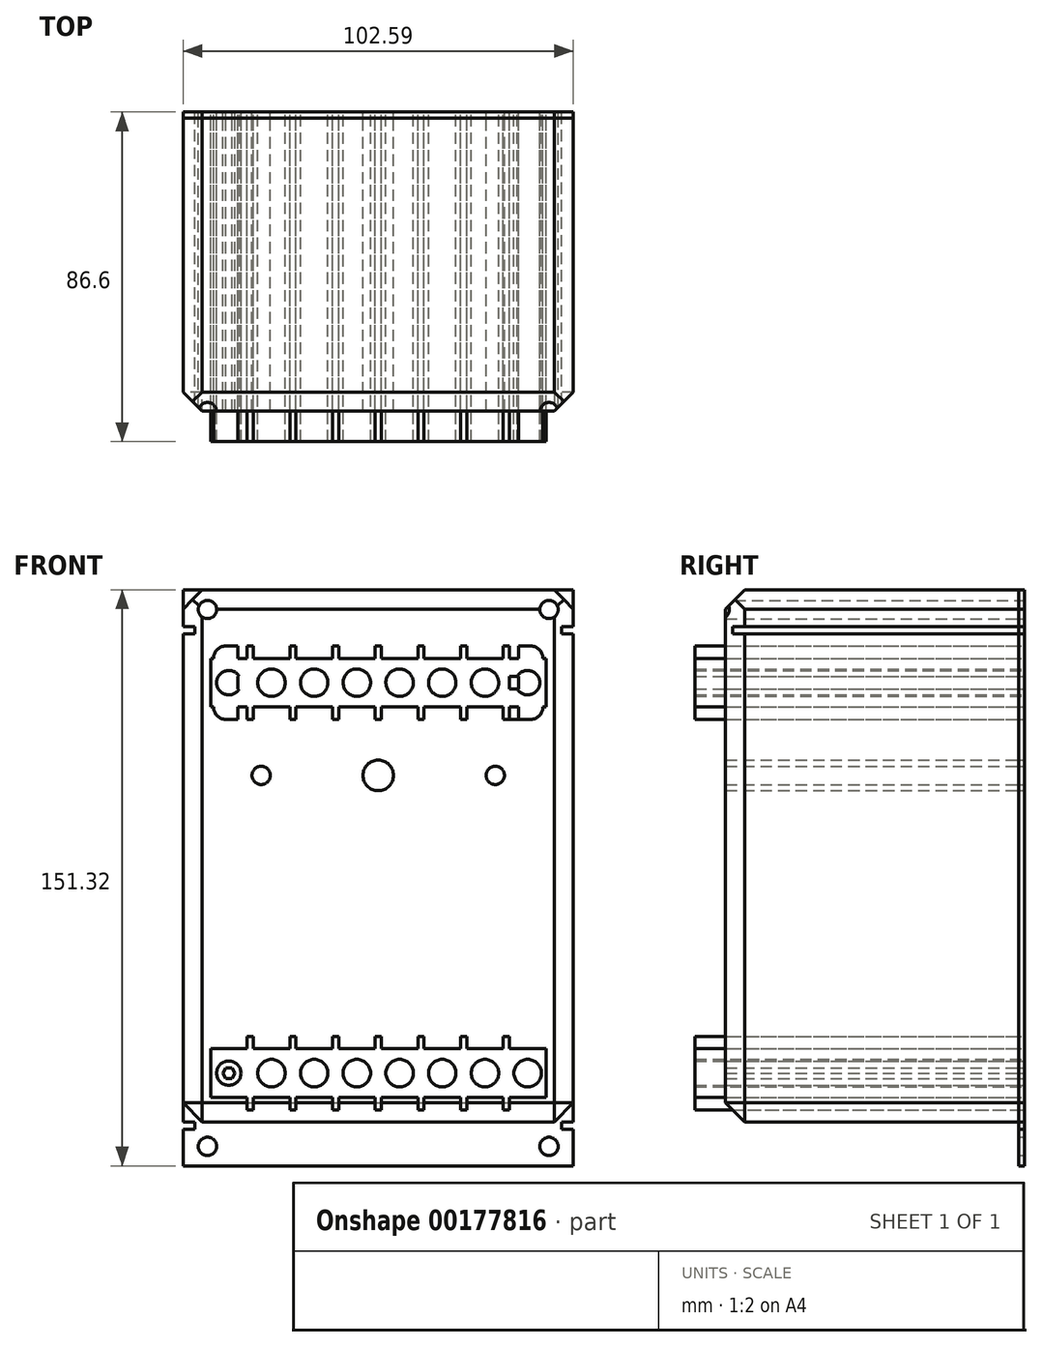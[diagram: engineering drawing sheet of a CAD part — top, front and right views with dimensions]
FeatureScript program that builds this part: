
annotation { "Feature Type Name" : "Feature", "Feature Type Description" : "" }
export const myFeature = defineFeature(function(context is Context, id is Id, definition is map)
    precondition{}
    {
        {
            var Q0;
            Q0=qCreatedBy(makeId("Front.planeOp"),FACE);
            var sketch = newSketch(context, id + "F0", { "sketchPlane" : qUnion([Q0])});
            skLineSegment(sketch, "E0", {"start": v(-127.7, 65.2) * mm, "end": v(-25.11, 65.2) * mm});
            skLineSegment(sketch, "E1", {"start": v(-25.11, 65.2) * mm, "end": v(-25.11, -63.04) * mm});
            skLineSegment(sketch, "E2", {"start": v(-25.11, -63.04) * mm, "end": v(-127.7, -63.04) * mm});
            skLineSegment(sketch, "E3", {"start": v(-127.7, -63.04) * mm, "end": v(-127.7, 65.2) * mm});
            skLineSegment(sketch, "E4", {"start": v(-127.7, 76.74) * mm, "end": v(-25.11, 76.74) * mm});
            skLineSegment(sketch, "E5", {"start": v(-25.11, -74.58) * mm, "end": v(-127.7, -74.58) * mm});
            skLineSegment(sketch, "E6", {"start": v(-127.7, 67.12) * mm, "end": v(-124.57, 67.12) * mm});
            skLineSegment(sketch, "E7", {"start": v(-25.11, -64.96) * mm, "end": v(-28.24, -64.96) * mm});
            skLineSegment(sketch, "E8", {"start": v(-124.57, -64.96) * mm, "end": v(-124.57, -63.04) * mm});
            skLineSegment(sketch, "E9", {"start": v(-28.24, -64.96) * mm, "end": v(-28.24, -63.04) * mm});
            skLineSegment(sketch, "E10", {"start": v(-127.7, 76.74) * mm, "end": v(-127.7, 67.12) * mm});
            skLineSegment(sketch, "E11", {"start": v(-124.57, 65.2) * mm, "end": v(-124.57, 67.12) * mm});
            skLineSegment(sketch, "E12", {"start": v(-28.24, 65.2) * mm, "end": v(-28.24, 67.12) * mm});
            skLineSegment(sketch, "E13", {"start": v(-25.11, 76.74) * mm, "end": v(-25.11, 67.12) * mm});
            skLineSegment(sketch, "E14", {"start": v(-28.24, 67.12) * mm, "end": v(-25.11, 67.12) * mm});
            skLineSegment(sketch, "E15", {"start": v(-127.7, -64.96) * mm, "end": v(-127.7, -74.58) * mm});
            skLineSegment(sketch, "E16", {"start": v(-25.11, -64.96) * mm, "end": v(-25.11, -74.58) * mm});
            skLineSegment(sketch, "E17", {"start": v(-124.57, -64.96) * mm, "end": v(-127.7, -64.96) * mm});
            skCircle(sketch, "E18", {"center": v(-121.29, 71.6) * mm, "radius": 2.41 * mm});
            skCircle(sketch, "E19", {"center": v(-31.52, 71.6) * mm, "radius": 2.41 * mm});
            skCircle(sketch, "E20", {"center": v(-121.29, -69.45) * mm, "radius": 2.41 * mm});
            skCircle(sketch, "E21", {"center": v(-31.52, -69.45) * mm, "radius": 2.41 * mm});
            skLineSegment(sketch, "E22", {"start": v(-102.11, 49.64) * mm, "end": v(-107.62, 54.1) * mm});
            skLineSegment(sketch, "E23", {"start": v(-101.3, 50.63) * mm, "end": v(-106.82, 55.1) * mm});
            skCircle(sketch, "E24", {"center": v(-104.46, 52.37) * mm, "radius": 3.6 * mm});
            skLineSegment(sketch, "E25", {"start": v(-90.88, 49.64) * mm, "end": v(-96.4, 54.1) * mm});
            skLineSegment(sketch, "E26", {"start": v(-90.07, 50.63) * mm, "end": v(-95.58, 55.1) * mm});
            skCircle(sketch, "E27", {"center": v(-93.23, 52.37) * mm, "radius": 3.6 * mm});
            skLineSegment(sketch, "E28", {"start": v(-79.67, 49.64) * mm, "end": v(-85.18, 54.1) * mm});
            skLineSegment(sketch, "E29", {"start": v(-78.86, 50.63) * mm, "end": v(-84.37, 55.1) * mm});
            skCircle(sketch, "E30", {"center": v(-82.02, 52.37) * mm, "radius": 3.6 * mm});
            skLineSegment(sketch, "E31", {"start": v(-68.44, 49.64) * mm, "end": v(-73.95, 54.1) * mm});
            skLineSegment(sketch, "E32", {"start": v(-67.63, 50.63) * mm, "end": v(-73.14, 55.1) * mm});
            skCircle(sketch, "E33", {"center": v(-70.79, 52.37) * mm, "radius": 3.6 * mm});
            skLineSegment(sketch, "E34", {"start": v(-57.23, 49.64) * mm, "end": v(-62.74, 54.1) * mm});
            skLineSegment(sketch, "E35", {"start": v(-56.42, 50.63) * mm, "end": v(-61.93, 55.1) * mm});
            skCircle(sketch, "E36", {"center": v(-59.58, 52.37) * mm, "radius": 3.6 * mm});
            skLineSegment(sketch, "E37", {"start": v(-46, 49.64) * mm, "end": v(-51.5, 54.1) * mm});
            skLineSegment(sketch, "E38", {"start": v(-45.19, 50.63) * mm, "end": v(-50.7, 55.1) * mm});
            skCircle(sketch, "E39", {"center": v(-48.35, 52.37) * mm, "radius": 3.6 * mm});
            skLineSegment(sketch, "E40", {"start": v(-120.47, 58.78) * mm, "end": v(-119.69, 58.78) * mm});
            skLineSegment(sketch, "E41", {"start": v(-120.47, 45.96) * mm, "end": v(-119.69, 45.96) * mm});
            skLineSegment(sketch, "E42", {"start": v(-110.87, 61.99) * mm, "end": v(-109.27, 61.99) * mm});
            skLineSegment(sketch, "E43", {"start": v(-110.87, 42.75) * mm, "end": v(-109.27, 42.75) * mm});
            skLineSegment(sketch, "E44", {"start": v(-109.27, 61.99) * mm, "end": v(-109.27, 42.75) * mm});
            skLineSegment(sketch, "E45", {"start": v(-110.87, 61.99) * mm, "end": v(-110.87, 42.75) * mm});
            skLineSegment(sketch, "E46", {"start": v(-98.03, 61.99) * mm, "end": v(-98.03, 42.75) * mm});
            skLineSegment(sketch, "E47", {"start": v(-99.64, 61.99) * mm, "end": v(-99.64, 42.75) * mm});
            skLineSegment(sketch, "E48", {"start": v(-88.43, 61.99) * mm, "end": v(-88.43, 42.75) * mm});
            skLineSegment(sketch, "E49", {"start": v(-86.83, 61.99) * mm, "end": v(-86.83, 42.75) * mm});
            skLineSegment(sketch, "E50", {"start": v(-77.2, 61.99) * mm, "end": v(-77.2, 42.75) * mm});
            skLineSegment(sketch, "E51", {"start": v(-75.6, 61.99) * mm, "end": v(-75.6, 42.75) * mm});
            skLineSegment(sketch, "E52", {"start": v(-65.99, 61.99) * mm, "end": v(-65.99, 42.75) * mm});
            skLineSegment(sketch, "E53", {"start": v(-64.38, 61.99) * mm, "end": v(-64.38, 42.75) * mm});
            skLineSegment(sketch, "E54", {"start": v(-54.75, 61.99) * mm, "end": v(-54.75, 42.75) * mm});
            skLineSegment(sketch, "E55", {"start": v(-53.15, 61.99) * mm, "end": v(-53.15, 42.75) * mm});
            skLineSegment(sketch, "E56", {"start": v(-43.55, 61.99) * mm, "end": v(-43.55, 42.75) * mm});
            skLineSegment(sketch, "E57", {"start": v(-41.94, 61.99) * mm, "end": v(-41.94, 42.75) * mm});
            skLineSegment(sketch, "E58", {"start": v(-120.47, 45.96) * mm, "end": v(-120.47, 58.78) * mm});
            skLineSegment(sketch, "E59", {"start": v(-32.34, 45.96) * mm, "end": v(-32.34, 58.78) * mm});
            skLineSegment(sketch, "E60", {"start": v(-41.94, 58.78) * mm, "end": v(-39.54, 58.78) * mm});
            skLineSegment(sketch, "E61", {"start": v(-43.55, 61.99) * mm, "end": v(-41.94, 61.99) * mm});
            skLineSegment(sketch, "E62", {"start": v(-53.15, 58.78) * mm, "end": v(-43.55, 58.78) * mm});
            skLineSegment(sketch, "E63", {"start": v(-54.75, 61.99) * mm, "end": v(-53.15, 61.99) * mm});
            skLineSegment(sketch, "E64", {"start": v(-64.38, 58.78) * mm, "end": v(-54.75, 58.78) * mm});
            skLineSegment(sketch, "E65", {"start": v(-65.99, 61.99) * mm, "end": v(-64.38, 61.99) * mm});
            skLineSegment(sketch, "E66", {"start": v(-75.6, 58.78) * mm, "end": v(-65.99, 58.78) * mm});
            skLineSegment(sketch, "E67", {"start": v(-77.2, 61.99) * mm, "end": v(-75.6, 61.99) * mm});
            skLineSegment(sketch, "E68", {"start": v(-86.83, 58.78) * mm, "end": v(-77.2, 58.78) * mm});
            skLineSegment(sketch, "E69", {"start": v(-88.43, 61.99) * mm, "end": v(-86.83, 61.99) * mm});
            skLineSegment(sketch, "E70", {"start": v(-98.03, 58.78) * mm, "end": v(-88.43, 58.78) * mm});
            skLineSegment(sketch, "E71", {"start": v(-99.64, 61.99) * mm, "end": v(-98.03, 61.99) * mm});
            skLineSegment(sketch, "E72", {"start": v(-109.27, 58.78) * mm, "end": v(-99.64, 58.78) * mm});
            skLineSegment(sketch, "E73", {"start": v(-99.64, 42.75) * mm, "end": v(-98.03, 42.75) * mm});
            skLineSegment(sketch, "E74", {"start": v(-98.03, 45.96) * mm, "end": v(-88.43, 45.96) * mm});
            skLineSegment(sketch, "E75", {"start": v(-88.43, 42.75) * mm, "end": v(-86.83, 42.75) * mm});
            skLineSegment(sketch, "E76", {"start": v(-86.83, 45.96) * mm, "end": v(-77.2, 45.96) * mm});
            skLineSegment(sketch, "E77", {"start": v(-77.2, 42.75) * mm, "end": v(-75.6, 42.75) * mm});
            skLineSegment(sketch, "E78", {"start": v(-75.6, 45.96) * mm, "end": v(-65.99, 45.96) * mm});
            skLineSegment(sketch, "E79", {"start": v(-65.99, 42.75) * mm, "end": v(-64.38, 42.75) * mm});
            skLineSegment(sketch, "E80", {"start": v(-64.38, 45.96) * mm, "end": v(-54.75, 45.96) * mm});
            skLineSegment(sketch, "E81", {"start": v(-54.75, 42.75) * mm, "end": v(-53.15, 42.75) * mm});
            skLineSegment(sketch, "E82", {"start": v(-53.15, 45.96) * mm, "end": v(-43.55, 45.96) * mm});
            skLineSegment(sketch, "E83", {"start": v(-43.55, 42.75) * mm, "end": v(-41.94, 42.75) * mm});
            skLineSegment(sketch, "E84", {"start": v(-41.94, 45.96) * mm, "end": v(-39.54, 45.96) * mm});
            skLineSegment(sketch, "E85", {"start": v(-109.27, 45.96) * mm, "end": v(-99.64, 45.96) * mm});
            skLineSegment(sketch, "E86", {"start": v(-109.27, -56.63) * mm, "end": v(-99.64, -56.63) * mm});
            skLineSegment(sketch, "E87", {"start": v(-41.94, -56.63) * mm, "end": v(-32.34, -56.63) * mm});
            skLineSegment(sketch, "E88", {"start": v(-43.55, -59.84) * mm, "end": v(-41.94, -59.84) * mm});
            skLineSegment(sketch, "E89", {"start": v(-53.15, -56.63) * mm, "end": v(-43.55, -56.63) * mm});
            skLineSegment(sketch, "E90", {"start": v(-54.75, -59.84) * mm, "end": v(-53.15, -59.84) * mm});
            skLineSegment(sketch, "E91", {"start": v(-64.38, -56.63) * mm, "end": v(-54.75, -56.63) * mm});
            skLineSegment(sketch, "E92", {"start": v(-65.99, -59.84) * mm, "end": v(-64.38, -59.84) * mm});
            skLineSegment(sketch, "E93", {"start": v(-75.6, -56.63) * mm, "end": v(-65.99, -56.63) * mm});
            skLineSegment(sketch, "E94", {"start": v(-77.2, -59.84) * mm, "end": v(-75.6, -59.84) * mm});
            skLineSegment(sketch, "E95", {"start": v(-86.83, -56.63) * mm, "end": v(-77.2, -56.63) * mm});
            skLineSegment(sketch, "E96", {"start": v(-88.43, -59.84) * mm, "end": v(-86.83, -59.84) * mm});
            skLineSegment(sketch, "E97", {"start": v(-98.03, -56.63) * mm, "end": v(-88.43, -56.63) * mm});
            skLineSegment(sketch, "E98", {"start": v(-99.64, -59.84) * mm, "end": v(-98.03, -59.84) * mm});
            skLineSegment(sketch, "E99", {"start": v(-109.27, -43.8) * mm, "end": v(-99.64, -43.8) * mm});
            skLineSegment(sketch, "E100", {"start": v(-99.64, -40.6) * mm, "end": v(-98.03, -40.6) * mm});
            skLineSegment(sketch, "E101", {"start": v(-98.03, -43.8) * mm, "end": v(-88.43, -43.8) * mm});
            skLineSegment(sketch, "E102", {"start": v(-88.43, -40.6) * mm, "end": v(-86.83, -40.6) * mm});
            skLineSegment(sketch, "E103", {"start": v(-86.83, -43.8) * mm, "end": v(-77.2, -43.8) * mm});
            skLineSegment(sketch, "E104", {"start": v(-77.2, -40.6) * mm, "end": v(-75.6, -40.6) * mm});
            skLineSegment(sketch, "E105", {"start": v(-75.6, -43.8) * mm, "end": v(-65.99, -43.8) * mm});
            skLineSegment(sketch, "E106", {"start": v(-65.99, -40.6) * mm, "end": v(-64.38, -40.6) * mm});
            skLineSegment(sketch, "E107", {"start": v(-64.38, -43.8) * mm, "end": v(-54.75, -43.8) * mm});
            skLineSegment(sketch, "E108", {"start": v(-54.75, -40.6) * mm, "end": v(-53.15, -40.6) * mm});
            skLineSegment(sketch, "E109", {"start": v(-53.15, -43.8) * mm, "end": v(-43.55, -43.8) * mm});
            skLineSegment(sketch, "E110", {"start": v(-43.55, -40.6) * mm, "end": v(-41.94, -40.6) * mm});
            skLineSegment(sketch, "E111", {"start": v(-41.94, -43.8) * mm, "end": v(-32.34, -43.8) * mm});
            skLineSegment(sketch, "E112", {"start": v(-32.34, -56.63) * mm, "end": v(-32.34, -43.8) * mm});
            skLineSegment(sketch, "E113", {"start": v(-120.47, -56.63) * mm, "end": v(-120.47, -43.8) * mm});
            skLineSegment(sketch, "E114", {"start": v(-41.94, -40.6) * mm, "end": v(-41.94, -59.84) * mm});
            skLineSegment(sketch, "E115", {"start": v(-43.55, -40.6) * mm, "end": v(-43.55, -59.84) * mm});
            skLineSegment(sketch, "E116", {"start": v(-53.15, -40.6) * mm, "end": v(-53.15, -59.84) * mm});
            skLineSegment(sketch, "E117", {"start": v(-54.75, -40.6) * mm, "end": v(-54.75, -59.84) * mm});
            skLineSegment(sketch, "E118", {"start": v(-64.38, -40.6) * mm, "end": v(-64.38, -59.84) * mm});
            skLineSegment(sketch, "E119", {"start": v(-65.99, -40.6) * mm, "end": v(-65.99, -59.84) * mm});
            skLineSegment(sketch, "E120", {"start": v(-75.6, -40.6) * mm, "end": v(-75.6, -59.84) * mm});
            skLineSegment(sketch, "E121", {"start": v(-77.2, -40.6) * mm, "end": v(-77.2, -59.84) * mm});
            skLineSegment(sketch, "E122", {"start": v(-86.83, -40.6) * mm, "end": v(-86.83, -59.84) * mm});
            skLineSegment(sketch, "E123", {"start": v(-88.43, -40.6) * mm, "end": v(-88.43, -59.84) * mm});
            skLineSegment(sketch, "E124", {"start": v(-99.64, -40.6) * mm, "end": v(-99.64, -59.84) * mm});
            skLineSegment(sketch, "E125", {"start": v(-98.03, -40.6) * mm, "end": v(-98.03, -59.84) * mm});
            skLineSegment(sketch, "E126", {"start": v(-110.87, -40.6) * mm, "end": v(-110.87, -59.84) * mm});
            skLineSegment(sketch, "E127", {"start": v(-109.27, -40.6) * mm, "end": v(-109.27, -59.84) * mm});
            skLineSegment(sketch, "E128", {"start": v(-110.87, -59.84) * mm, "end": v(-109.27, -59.84) * mm});
            skLineSegment(sketch, "E129", {"start": v(-110.87, -40.6) * mm, "end": v(-109.27, -40.6) * mm});
            skLineSegment(sketch, "E130", {"start": v(-120.47, -56.63) * mm, "end": v(-110.87, -56.63) * mm});
            skLineSegment(sketch, "E131", {"start": v(-120.47, -43.8) * mm, "end": v(-110.87, -43.8) * mm});
            skCircle(sketch, "E132", {"center": v(-37.14, -50.22) * mm, "radius": 3.6 * mm});
            skLineSegment(sketch, "E133", {"start": v(-33.98, -51.96) * mm, "end": v(-39.5, -47.48) * mm});
            skLineSegment(sketch, "E134", {"start": v(-34.79, -52.95) * mm, "end": v(-40.3, -48.48) * mm});
            skCircle(sketch, "E135", {"center": v(-48.35, -50.22) * mm, "radius": 3.6 * mm});
            skLineSegment(sketch, "E136", {"start": v(-45.19, -51.96) * mm, "end": v(-50.7, -47.48) * mm});
            skLineSegment(sketch, "E137", {"start": v(-46, -52.95) * mm, "end": v(-51.5, -48.48) * mm});
            skCircle(sketch, "E138", {"center": v(-59.58, -50.22) * mm, "radius": 3.6 * mm});
            skLineSegment(sketch, "E139", {"start": v(-56.42, -51.96) * mm, "end": v(-61.93, -47.48) * mm});
            skLineSegment(sketch, "E140", {"start": v(-57.23, -52.95) * mm, "end": v(-62.74, -48.48) * mm});
            skCircle(sketch, "E141", {"center": v(-70.79, -50.22) * mm, "radius": 3.6 * mm});
            skLineSegment(sketch, "E142", {"start": v(-67.63, -51.96) * mm, "end": v(-73.14, -47.48) * mm});
            skLineSegment(sketch, "E143", {"start": v(-68.44, -52.95) * mm, "end": v(-73.95, -48.48) * mm});
            skCircle(sketch, "E144", {"center": v(-82.02, -50.22) * mm, "radius": 3.6 * mm});
            skLineSegment(sketch, "E145", {"start": v(-78.86, -51.96) * mm, "end": v(-84.37, -47.48) * mm});
            skLineSegment(sketch, "E146", {"start": v(-79.67, -52.95) * mm, "end": v(-85.18, -48.48) * mm});
            skCircle(sketch, "E147", {"center": v(-93.23, -50.22) * mm, "radius": 3.6 * mm});
            skLineSegment(sketch, "E148", {"start": v(-90.07, -51.96) * mm, "end": v(-95.58, -47.48) * mm});
            skLineSegment(sketch, "E149", {"start": v(-90.88, -52.95) * mm, "end": v(-96.4, -48.48) * mm});
            skCircle(sketch, "E150", {"center": v(-104.46, -50.22) * mm, "radius": 3.6 * mm});
            skLineSegment(sketch, "E151", {"start": v(-101.3, -51.96) * mm, "end": v(-106.82, -47.48) * mm});
            skLineSegment(sketch, "E152", {"start": v(-102.11, -52.95) * mm, "end": v(-107.62, -48.48) * mm});
            skCircle(sketch, "E153", {"center": v(-107.18, 28) * mm, "radius": 4 * mm});
            skCircle(sketch, "E154", {"center": v(-107.18, 28) * mm, "radius": 2.4 * mm});
            skCircle(sketch, "E155", {"center": v(-45.63, 28) * mm, "radius": 4 * mm});
            skCircle(sketch, "E156", {"center": v(-45.63, 28) * mm, "radius": 2.4 * mm});
            skCircle(sketch, "E157", {"center": v(-76.4, 28) * mm, "radius": 4 * mm});
            skCircle(sketch, "E158", {"center": v(-107.18, 1.08) * mm, "radius": 3.6 * mm});
            skLineSegment(sketch, "E159", {"start": v(-81.92, 12.95) * mm, "end": v(-81.92, 2.03) * mm});
            skLineSegment(sketch, "E160", {"start": v(-70.9, 12.95) * mm, "end": v(-70.9, 2.03) * mm});
            skLineSegment(sketch, "E161", {"start": v(-81.92, 12.95) * mm, "end": v(-70.9, 12.95) * mm});
            skLineSegment(sketch, "E162", {"start": v(-81.92, 2.03) * mm, "end": v(-70.9, 2.03) * mm});
            skCircle(sketch, "E163", {"center": v(-115.67, -50.22) * mm, "radius": 3.2 * mm});
            skLineSegment(sketch, "E164", {"start": v(-116.47, -48.83) * mm, "end": v(-117.27, -50.22) * mm});
            skLineSegment(sketch, "E165", {"start": v(-117.27, -50.22) * mm, "end": v(-116.47, -51.6) * mm});
            skLineSegment(sketch, "E166", {"start": v(-116.47, -51.6) * mm, "end": v(-114.87, -51.6) * mm});
            skLineSegment(sketch, "E167", {"start": v(-114.87, -51.6) * mm, "end": v(-114.07, -50.22) * mm});
            skLineSegment(sketch, "E168", {"start": v(-114.07, -50.22) * mm, "end": v(-114.87, -48.83) * mm});
            skLineSegment(sketch, "E169", {"start": v(-114.87, -48.83) * mm, "end": v(-116.47, -48.83) * mm});
            skArc(sketch, "E170", {"start": v(-112.9, 53.97) * mm, "mid": v(-118.88, 52.37) * mm, "end": v(-112.9, 50.77) * mm});
            skLineSegment(sketch, "E171", {"start": v(-116.47, 53.76) * mm, "end": v(-117.27, 52.37) * mm});
            skLineSegment(sketch, "E172", {"start": v(-117.27, 52.37) * mm, "end": v(-116.47, 50.98) * mm});
            skLineSegment(sketch, "E173", {"start": v(-116.47, 50.98) * mm, "end": v(-114.87, 50.98) * mm});
            skLineSegment(sketch, "E174", {"start": v(-114.87, 50.98) * mm, "end": v(-114.07, 52.37) * mm});
            skLineSegment(sketch, "E175", {"start": v(-114.07, 52.37) * mm, "end": v(-114.87, 53.76) * mm});
            skLineSegment(sketch, "E176", {"start": v(-114.87, 53.76) * mm, "end": v(-116.47, 53.76) * mm});
            skArc(sketch, "E177", {"start": v(-39.92, 50.77) * mm, "mid": v(-33.93, 52.37) * mm, "end": v(-39.92, 53.97) * mm});
            skLineSegment(sketch, "E178", {"start": v(-37.94, 53.76) * mm, "end": v(-38.74, 52.37) * mm});
            skLineSegment(sketch, "E179", {"start": v(-38.74, 52.37) * mm, "end": v(-37.94, 50.98) * mm});
            skLineSegment(sketch, "E180", {"start": v(-37.94, 50.98) * mm, "end": v(-36.34, 50.98) * mm});
            skLineSegment(sketch, "E181", {"start": v(-36.34, 50.98) * mm, "end": v(-35.54, 52.37) * mm});
            skLineSegment(sketch, "E182", {"start": v(-35.54, 52.37) * mm, "end": v(-36.34, 53.76) * mm});
            skLineSegment(sketch, "E183", {"start": v(-36.34, 53.76) * mm, "end": v(-37.94, 53.76) * mm});
            skLineSegment(sketch, "E184", {"start": v(-107.18, 4.68) * mm, "end": v(-107.18, 7.41) * mm});
            skLineSegment(sketch, "E185", {"start": v(-110.61, 2.2) * mm, "end": v(-113.21, 3.04) * mm});
            skLineSegment(sketch, "E186", {"start": v(-109.3, -1.84) * mm, "end": v(-110.9, -4.05) * mm});
            skLineSegment(sketch, "E187", {"start": v(-105.06, -1.84) * mm, "end": v(-103.46, -4.05) * mm});
            skLineSegment(sketch, "E188", {"start": v(-103.75, 2.2) * mm, "end": v(-101.16, 3.04) * mm});
            skLineSegment(sketch, "E189", {"start": v(41.36, 42.75) * mm, "end": v(49.78, 42.11) * mm});
            skLineSegment(sketch, "E190", {"start": v(41.36, 55.58) * mm, "end": v(49.78, 56.22) * mm});
            skLineSegment(sketch, "E191", {"start": v(34.52, 50.77) * mm, "end": v(34.52, 55.58) * mm});
            skLineSegment(sketch, "E192", {"start": v(32.55, 39.55) * mm, "end": v(39.76, 39.55) * mm});
            skLineSegment(sketch, "E193", {"start": v(32.55, 58.78) * mm, "end": v(39.68, 58.78) * mm});
            skLineSegment(sketch, "E194", {"start": v(29.34, 55.58) * mm, "end": v(29.34, 58.78) * mm});
            skLineSegment(sketch, "E195", {"start": v(29.34, 47.56) * mm, "end": v(29.34, 50.77) * mm});
            skLineSegment(sketch, "E196", {"start": v(32.55, 39.55) * mm, "end": v(32.55, 42.75) * mm});
            skLineSegment(sketch, "E197", {"start": v(29.34, 39.55) * mm, "end": v(29.34, 42.75) * mm});
            skLineSegment(sketch, "E198", {"start": v(41.36, 39.55) * mm, "end": v(44.25, 39.55) * mm});
            skLineSegment(sketch, "E199", {"start": v(41.36, 39.55) * mm, "end": v(41.36, 58.78) * mm});
            skLineSegment(sketch, "E200", {"start": v(29.34, 39.55) * mm, "end": v(32.55, 39.55) * mm});
            skLineSegment(sketch, "E201", {"start": v(29.34, 42.75) * mm, "end": v(39.76, 42.75) * mm});
            skLineSegment(sketch, "E202", {"start": v(29.34, 47.56) * mm, "end": v(36.82, 47.56) * mm});
            skLineSegment(sketch, "E203", {"start": v(29.34, 50.77) * mm, "end": v(36.82, 50.77) * mm});
            skLineSegment(sketch, "E204", {"start": v(29.34, 55.58) * mm, "end": v(39.76, 55.58) * mm});
            skLineSegment(sketch, "E205", {"start": v(29.34, 58.78) * mm, "end": v(32.55, 58.78) * mm});
            skLineSegment(sketch, "E206", {"start": v(-113.27, 50.77) * mm, "end": v(-110.87, 50.77) * mm});
            skLineSegment(sketch, "E207", {"start": v(-113.27, 53.97) * mm, "end": v(-110.87, 53.97) * mm});
            skLineSegment(sketch, "E208", {"start": v(-41.94, 53.97) * mm, "end": v(-41.94, 50.77) * mm});
            skLineSegment(sketch, "E209", {"start": v(-39.54, 53.97) * mm, "end": v(-39.54, 50.77) * mm});
            skLineSegment(sketch, "E210", {"start": v(-41.94, 45.96) * mm, "end": v(-41.94, 42.75) * mm});
            skLineSegment(sketch, "E211", {"start": v(-39.54, 45.96) * mm, "end": v(-39.54, 42.75) * mm});
            skLineSegment(sketch, "E212", {"start": v(-39.54, 42.75) * mm, "end": v(-41.94, 42.75) * mm});
            skLineSegment(sketch, "E213", {"start": v(-39.54, 61.99) * mm, "end": v(-41.94, 61.99) * mm});
            skLineSegment(sketch, "E214", {"start": v(-113.27, 53.97) * mm, "end": v(-113.27, 50.77) * mm});
            skLineSegment(sketch, "E215", {"start": v(-113.27, 45.96) * mm, "end": v(-113.27, 42.75) * mm});
            skLineSegment(sketch, "E216", {"start": v(-110.87, 45.96) * mm, "end": v(-110.87, 42.75) * mm});
            skLineSegment(sketch, "E217", {"start": v(-110.87, 53.97) * mm, "end": v(-110.87, 50.77) * mm});
            skLineSegment(sketch, "E218", {"start": v(-41.94, 50.77) * mm, "end": v(-39.54, 50.77) * mm});
            skLineSegment(sketch, "E219", {"start": v(-41.94, 53.97) * mm, "end": v(-39.54, 53.97) * mm});
            skLineSegment(sketch, "E220", {"start": v(-113.27, 45.96) * mm, "end": v(-110.87, 45.96) * mm});
            skLineSegment(sketch, "E221", {"start": v(-113.27, 58.78) * mm, "end": v(-110.87, 58.78) * mm});
            skLineSegment(sketch, "E222", {"start": v(-113.27, 42.75) * mm, "end": v(-110.87, 42.75) * mm});
            skLineSegment(sketch, "E223", {"start": v(-113.27, 61.99) * mm, "end": v(-110.87, 61.99) * mm});
            skLineSegment(sketch, "E224", {"start": v(-110.87, 61.99) * mm, "end": v(-110.87, 58.78) * mm});
            skLineSegment(sketch, "E225", {"start": v(-41.94, 61.99) * mm, "end": v(-41.94, 58.78) * mm});
            skArc(sketch, "E226", {"start": v(-119.69, 45.96) * mm, "mid": v(-118.75, 43.7) * mm, "end": v(-116.48, 42.75) * mm});
            skArc(sketch, "E227", {"start": v(-36.33, 42.75) * mm, "mid": v(-34.07, 43.7) * mm, "end": v(-33.13, 45.96) * mm});
            skArc(sketch, "E228", {"start": v(-33.13, 58.78) * mm, "mid": v(-34.07, 61.05) * mm, "end": v(-36.33, 61.99) * mm});
            skArc(sketch, "E229", {"start": v(-116.48, 61.99) * mm, "mid": v(-118.75, 61.05) * mm, "end": v(-119.69, 58.78) * mm});
            skLineSegment(sketch, "E230", {"start": v(-119.69, 58.78) * mm, "end": v(-119.69, 45.96) * mm});
            skLineSegment(sketch, "E231", {"start": v(-33.13, 58.78) * mm, "end": v(-33.13, 45.96) * mm});
            skLineSegment(sketch, "E232", {"start": v(-113.27, 61.99) * mm, "end": v(-113.27, 58.78) * mm});
            skLineSegment(sketch, "E233", {"start": v(-39.54, 61.99) * mm, "end": v(-39.54, 58.78) * mm});
            skArc(sketch, "E234", {"start": v(38.15, 52.77) * mm, "mid": v(36.55, 49.16) * mm, "end": v(38.15, 45.56) * mm});
            skLineSegment(sketch, "E235", {"start": v(34.52, 42.75) * mm, "end": v(34.52, 47.56) * mm});
            skLineSegment(sketch, "E236", {"start": v(39.76, 39.55) * mm, "end": v(39.76, 58.78) * mm});
            skLineSegment(sketch, "E237", {"start": v(38.15, 45.56) * mm, "end": v(39.76, 45.56) * mm});
            skLineSegment(sketch, "E238", {"start": v(38.15, 52.77) * mm, "end": v(39.76, 52.77) * mm});
            skLineSegment(sketch, "E239", {"start": v(35.75, 39.55) * mm, "end": v(49.78, 39.55) * mm});
            skLineSegment(sketch, "E240", {"start": v(35.75, 58.78) * mm, "end": v(49.78, 58.78) * mm});
            skLineSegment(sketch, "E241", {"start": v(126.73, -64.96) * mm, "end": v(128.32, -64.96) * mm});
            skLineSegment(sketch, "E242", {"start": v(126.73, 67.12) * mm, "end": v(128.32, 67.12) * mm});
            skLineSegment(sketch, "E243", {"start": v(126.73, 55.58) * mm, "end": v(126.73, 76.74) * mm});
            skLineSegment(sketch, "E244", {"start": v(59.4, -52.15) * mm, "end": v(59.4, 54.3) * mm});
            skLineSegment(sketch, "E245", {"start": v(60.67, -53.42) * mm, "end": v(68.4, -53.42) * mm});
            skLineSegment(sketch, "E246", {"start": v(60.67, -53.42) * mm, "end": v(126.73, -53.42) * mm});
            skLineSegment(sketch, "E247", {"start": v(60.67, -53.42) * mm, "end": v(52.17, -61.93) * mm});
            skLineSegment(sketch, "E248", {"start": v(59.4, -52.15) * mm, "end": v(50.9, -60.66) * mm});
            skLineSegment(sketch, "E249", {"start": v(50.9, -61.93) * mm, "end": v(52.17, -61.93) * mm});
            skLineSegment(sketch, "E250", {"start": v(50.9, -61.93) * mm, "end": v(50.9, -60.66) * mm});
            skCircle(sketch, "E251", {"center": v(81.2, -58.23) * mm, "radius": 4.4 * mm});
            skCircle(sketch, "E252", {"center": v(81.2, -58.23) * mm, "radius": 3.62 * mm});
            skLineSegment(sketch, "E253", {"start": v(80.6, -59.27) * mm, "end": v(80, -58.23) * mm});
            skLineSegment(sketch, "E254", {"start": v(80, -58.23) * mm, "end": v(80.6, -57.2) * mm});
            skLineSegment(sketch, "E255", {"start": v(80.6, -57.2) * mm, "end": v(81.8, -57.2) * mm});
            skLineSegment(sketch, "E256", {"start": v(81.8, -57.2) * mm, "end": v(82.4, -58.23) * mm});
            skLineSegment(sketch, "E257", {"start": v(82.4, -58.23) * mm, "end": v(81.8, -59.27) * mm});
            skLineSegment(sketch, "E258", {"start": v(81.8, -59.27) * mm, "end": v(80.6, -59.27) * mm});
            skLineSegment(sketch, "E259", {"start": v(60.67, 55.58) * mm, "end": v(126.73, 55.58) * mm});
            skLineSegment(sketch, "E260", {"start": v(80.6, 61.43) * mm, "end": v(80, 60.39) * mm});
            skLineSegment(sketch, "E261", {"start": v(80, 60.39) * mm, "end": v(80.6, 59.34) * mm});
            skLineSegment(sketch, "E262", {"start": v(80.6, 59.34) * mm, "end": v(81.8, 59.34) * mm});
            skLineSegment(sketch, "E263", {"start": v(81.8, 59.34) * mm, "end": v(82.4, 60.39) * mm});
            skLineSegment(sketch, "E264", {"start": v(82.4, 60.39) * mm, "end": v(81.8, 61.43) * mm});
            skLineSegment(sketch, "E265", {"start": v(81.8, 61.43) * mm, "end": v(80.6, 61.43) * mm});
            skCircle(sketch, "E266", {"center": v(81.2, 60.39) * mm, "radius": 3.62 * mm});
            skCircle(sketch, "E267", {"center": v(81.2, 60.39) * mm, "radius": 4.4 * mm});
            skLineSegment(sketch, "E268", {"start": v(50.9, 64.08) * mm, "end": v(50.9, 62.81) * mm});
            skLineSegment(sketch, "E269", {"start": v(50.9, 64.08) * mm, "end": v(52.17, 64.08) * mm});
            skLineSegment(sketch, "E270", {"start": v(59.4, 54.3) * mm, "end": v(50.9, 62.81) * mm});
            skLineSegment(sketch, "E271", {"start": v(60.67, 55.58) * mm, "end": v(52.17, 64.08) * mm});
            skLineSegment(sketch, "E272", {"start": v(49.78, -63.04) * mm, "end": v(49.78, 65.2) * mm});
            skLineSegment(sketch, "E273", {"start": v(49.78, -63.04) * mm, "end": v(126.73, -63.04) * mm});
            skLineSegment(sketch, "E274", {"start": v(49.78, 65.2) * mm, "end": v(126.73, 65.2) * mm});
            skLineSegment(sketch, "E275", {"start": v(126.73, -74.58) * mm, "end": v(126.73, -53.42) * mm});
            skLineSegment(sketch, "E276", {"start": v(128.32, -74.58) * mm, "end": v(128.32, 76.74) * mm});
            skLineSegment(sketch, "E277", {"start": v(126.73, -74.58) * mm, "end": v(128.32, -74.58) * mm});
            skLineSegment(sketch, "E278", {"start": v(126.73, 76.74) * mm, "end": v(128.32, 76.74) * mm});
            skLineSegment(sketch, "E279", {"start": v(-116.48, 61.99) * mm, "end": v(-113.27, 61.99) * mm});
            skLineSegment(sketch, "E280", {"start": v(-116.48, 42.75) * mm, "end": v(-113.27, 42.75) * mm});
            skLineSegment(sketch, "E281", {"start": v(-36.33, 61.99) * mm, "end": v(-39.54, 61.99) * mm});
            skLineSegment(sketch, "E282", {"start": v(-36.33, 42.75) * mm, "end": v(-39.54, 42.75) * mm});
            skLineSegment(sketch, "E283", {"start": v(-33.13, 45.96) * mm, "end": v(-32.34, 45.96) * mm});
            skLineSegment(sketch, "E284", {"start": v(-33.13, 58.78) * mm, "end": v(-32.34, 58.78) * mm});
            skLineSegment(sketch, "E285", {"start": v(-111.64, 58.78) * mm, "end": v(-111.64, 53.97) * mm});
            skLineSegment(sketch, "E286", {"start": v(-41.17, 58.78) * mm, "end": v(-41.17, 53.97) * mm});
            skLineSegment(sketch, "E287", {"start": v(-41.17, 50.77) * mm, "end": v(-41.17, 45.96) * mm});
            skLineSegment(sketch, "E288", {"start": v(-111.64, 50.77) * mm, "end": v(-111.64, 45.96) * mm});
            skLineSegment(sketch, "E289", {"start": v(35.8, -40.6) * mm, "end": v(49.78, -40.6) * mm});
            skLineSegment(sketch, "E290", {"start": v(35.8, -59.84) * mm, "end": v(49.78, -59.84) * mm});
            skLineSegment(sketch, "E291", {"start": v(38.15, -46.61) * mm, "end": v(39.76, -46.61) * mm});
            skLineSegment(sketch, "E292", {"start": v(38.15, -53.82) * mm, "end": v(39.76, -53.82) * mm});
            skLineSegment(sketch, "E293", {"start": v(36.87, -51.96) * mm, "end": v(38.15, -51.96) * mm});
            skLineSegment(sketch, "E294", {"start": v(37.4, -52.95) * mm, "end": v(38.15, -52.95) * mm});
            skLineSegment(sketch, "E295", {"start": v(38.15, -52.95) * mm, "end": v(38.15, -51.96) * mm});
            skArc(sketch, "E296", {"start": v(38.15, -46.61) * mm, "mid": v(36.55, -50.22) * mm, "end": v(38.15, -53.82) * mm});
            skLineSegment(sketch, "E297", {"start": v(41.36, -56.63) * mm, "end": v(41.36, -43.8) * mm});
            skLineSegment(sketch, "E298", {"start": v(34.52, -58.55) * mm, "end": v(34.52, -41.88) * mm});
            skLineSegment(sketch, "E299", {"start": v(41.36, -43.8) * mm, "end": v(49.78, -43.16) * mm});
            skLineSegment(sketch, "E300", {"start": v(41.36, -56.63) * mm, "end": v(49.78, -57.27) * mm});
            skLineSegment(sketch, "E301", {"start": v(39.76, -46.61) * mm, "end": v(39.76, -53.88) * mm});
            skLineSegment(sketch, "E302", {"start": v(39.94, -46.61) * mm, "end": v(39.94, -53.88) * mm});
            skLineSegment(sketch, "E303", {"start": v(39.94, -46.61) * mm, "end": v(41.36, -46.61) * mm});
            skLineSegment(sketch, "E304", {"start": v(39.94, -53.88) * mm, "end": v(41.36, -53.88) * mm});
            skLineSegment(sketch, "E305", {"start": v(39.94, -50.24) * mm, "end": v(41.36, -50.24) * mm});
            skArc(sketch, "E306", {"start": v(35.8, -40.6) * mm, "mid": v(34.9, -40.98) * mm, "end": v(34.52, -41.88) * mm});
            skArc(sketch, "E307", {"start": v(34.52, -58.55) * mm, "mid": v(34.9, -59.46) * mm, "end": v(35.8, -59.84) * mm});
            skLineSegment(sketch, "E308", {"start": v(32.55, 47.56) * mm, "end": v(32.55, 50.77) * mm});
            skLineSegment(sketch, "E309", {"start": v(32.55, 55.58) * mm, "end": v(32.55, 58.78) * mm});
            skLineSegment(sketch, "E310", {"start": v(-23.77, 64.66) * mm, "end": v(-25.11, 64.66) * mm});
            skLineSegment(sketch, "E311", {"start": v(-23.77, 56.11) * mm, "end": v(-25.11, 56.11) * mm});
            skLineSegment(sketch, "E312", {"start": v(-23.5, 64.4) * mm, "end": v(-23.5, 56.37) * mm});
            skArc(sketch, "E313", {"start": v(-23.5, 56.9) * mm, "mid": v(-21.9, 60.39) * mm, "end": v(-23.5, 63.87) * mm});
            skArc(sketch, "E314", {"start": v(-23.5, 64.4) * mm, "mid": v(-23.58, 64.58) * mm, "end": v(-23.77, 64.66) * mm});
            skArc(sketch, "E315", {"start": v(-23.77, 56.11) * mm, "mid": v(-23.58, 56.19) * mm, "end": v(-23.5, 56.37) * mm});
            skArc(sketch, "E316", {"start": v(-23.77, -62.5) * mm, "mid": v(-23.58, -62.43) * mm, "end": v(-23.5, -62.25) * mm});
            skArc(sketch, "E317", {"start": v(-23.5, -54.22) * mm, "mid": v(-23.58, -54.04) * mm, "end": v(-23.77, -53.96) * mm});
            skArc(sketch, "E318", {"start": v(-23.5, -61.72) * mm, "mid": v(-21.9, -58.23) * mm, "end": v(-23.5, -54.75) * mm});
            skLineSegment(sketch, "E319", {"start": v(-23.5, -54.22) * mm, "end": v(-23.5, -62.25) * mm});
            skLineSegment(sketch, "E320", {"start": v(-23.77, -62.5) * mm, "end": v(-25.11, -62.5) * mm});
            skLineSegment(sketch, "E321", {"start": v(-23.77, -53.96) * mm, "end": v(-25.11, -53.96) * mm});
            skLineSegment(sketch, "E322", {"start": v(-129.05, -53.96) * mm, "end": v(-127.7, -53.96) * mm});
            skLineSegment(sketch, "E323", {"start": v(-129.05, -62.5) * mm, "end": v(-127.7, -62.5) * mm});
            skLineSegment(sketch, "E324", {"start": v(-129.3, -54.22) * mm, "end": v(-129.3, -62.25) * mm});
            skArc(sketch, "E325", {"start": v(-129.3, -54.75) * mm, "mid": v(-130.9, -58.23) * mm, "end": v(-129.3, -61.72) * mm});
            skArc(sketch, "E326", {"start": v(-129.05, -53.96) * mm, "mid": v(-129.23, -54.04) * mm, "end": v(-129.3, -54.22) * mm});
            skArc(sketch, "E327", {"start": v(-129.3, -62.25) * mm, "mid": v(-129.23, -62.43) * mm, "end": v(-129.05, -62.5) * mm});
            skArc(sketch, "E328", {"start": v(-129.3, 56.37) * mm, "mid": v(-129.23, 56.19) * mm, "end": v(-129.05, 56.11) * mm});
            skArc(sketch, "E329", {"start": v(-129.05, 64.66) * mm, "mid": v(-129.23, 64.58) * mm, "end": v(-129.3, 64.4) * mm});
            skArc(sketch, "E330", {"start": v(-129.3, 63.87) * mm, "mid": v(-130.9, 60.39) * mm, "end": v(-129.3, 56.9) * mm});
            skLineSegment(sketch, "E331", {"start": v(-129.3, 64.4) * mm, "end": v(-129.3, 56.37) * mm});
            skLineSegment(sketch, "E332", {"start": v(-129.05, 56.11) * mm, "end": v(-127.7, 56.11) * mm});
            skLineSegment(sketch, "E333", {"start": v(-129.05, 64.66) * mm, "end": v(-127.7, 64.66) * mm});
            skLineSegment(sketch, "E334", {"start": v(-32.8, -69.45) * mm, "end": v(-30.24, -69.45) * mm});
            skLineSegment(sketch, "E335", {"start": v(-31.52, -70.74) * mm, "end": v(-31.52, -68.17) * mm});
            skLineSegment(sketch, "E336", {"start": v(-122.57, -69.45) * mm, "end": v(-120, -69.45) * mm});
            skLineSegment(sketch, "E337", {"start": v(-121.29, -70.74) * mm, "end": v(-121.29, -68.17) * mm});
            skLineSegment(sketch, "E338", {"start": v(-28.64, -69.45) * mm, "end": v(-26.4, -69.45) * mm});
            skLineSegment(sketch, "E339", {"start": v(48.76, 32.01) * mm, "end": v(49.78, 32.01) * mm});
            skLineSegment(sketch, "E340", {"start": v(48.76, 24) * mm, "end": v(49.78, 24) * mm});
            skLineSegment(sketch, "E341", {"start": v(46.57, 30.41) * mm, "end": v(48.76, 30.41) * mm});
            skLineSegment(sketch, "E342", {"start": v(46.57, 25.6) * mm, "end": v(48.76, 25.6) * mm});
            skLineSegment(sketch, "E343", {"start": v(48.76, 24) * mm, "end": v(48.76, 32.01) * mm});
            skArc(sketch, "E344", {"start": v(46.57, 30.41) * mm, "mid": v(45.02, 28) * mm, "end": v(46.57, 25.6) * mm});
            skLineSegment(sketch, "E345", {"start": v(47.73, 12.95) * mm, "end": v(49.78, 12.95) * mm});
            skLineSegment(sketch, "E346", {"start": v(47.73, 2.03) * mm, "end": v(49.78, 2.03) * mm});
            skLineSegment(sketch, "E347", {"start": v(48.55, -2.53) * mm, "end": v(48.55, 2.03) * mm});
            skLineSegment(sketch, "E348", {"start": v(47.73, 2.03) * mm, "end": v(47.73, 12.95) * mm});
            skLineSegment(sketch, "E349", {"start": v(48.55, -2.53) * mm, "end": v(49.78, -2.53) * mm});
            skLineSegment(sketch, "E350", {"start": v(47.32, -2.27) * mm, "end": v(48.55, -2.27) * mm});
            skLineSegment(sketch, "E351", {"start": v(47.32, -2.27) * mm, "end": v(47.32, 4.68) * mm});
            skLineSegment(sketch, "E352", {"start": v(47.32, 4.68) * mm, "end": v(47.73, 4.68) * mm});
            skArc(sketch, "E353", {"start": v(-109.17, -0.76) * mm, "mid": v(-108.99, -0.94) * mm, "end": v(-108.79, -1.1) * mm});
            skLineSegment(sketch, "E354", {"start": v(-109.17, -0.76) * mm, "end": v(-105.58, 3.26) * mm});
            skLineSegment(sketch, "E355", {"start": v(-108.79, -1.1) * mm, "end": v(-105.2, 2.91) * mm});
            skLineSegment(sketch, "E356", {"start": v(-108.57, 0.68) * mm, "end": v(-108.19, 0.34) * mm});
            skLineSegment(sketch, "E357", {"start": v(-108.57, 0.68) * mm, "end": v(-109.17, -0.76) * mm});
            skLineSegment(sketch, "E358", {"start": v(-107.42, -0.34) * mm, "end": v(-108.79, -1.1) * mm});
            skLineSegment(sketch, "E359", {"start": v(-107.8, 0) * mm, "end": v(-107.42, -0.34) * mm});
            skLineSegment(sketch, "E360", {"start": v(-76.4, 12.95) * mm, "end": v(-76.4, 2.03) * mm});
            skLineSegment(sketch, "E361", {"start": v(-72.05, 10.39) * mm, "end": v(-72.05, 4.6) * mm});
            skLineSegment(sketch, "E362", {"start": v(-75.25, 10.39) * mm, "end": v(-75.25, 4.6) * mm});
            skLineSegment(sketch, "E363", {"start": v(-77.56, 10.39) * mm, "end": v(-77.56, 4.6) * mm});
            skLineSegment(sketch, "E364", {"start": v(-80.77, 10.39) * mm, "end": v(-80.77, 4.6) * mm});
            skLineSegment(sketch, "E365", {"start": v(-80.77, 10.39) * mm, "end": v(-77.56, 10.39) * mm});
            skLineSegment(sketch, "E366", {"start": v(-80.77, 4.6) * mm, "end": v(-77.56, 4.6) * mm});
            skLineSegment(sketch, "E367", {"start": v(-75.25, 10.39) * mm, "end": v(-72.05, 10.39) * mm});
            skLineSegment(sketch, "E368", {"start": v(-75.25, 4.6) * mm, "end": v(-72.05, 4.6) * mm});
            skLineSegment(sketch, "E369", {"start": v(-80.77, 6.52) * mm, "end": v(-77.56, 6.52) * mm});
            skLineSegment(sketch, "E370", {"start": v(-80.77, 8.45) * mm, "end": v(-77.56, 8.45) * mm});
            skLineSegment(sketch, "E371", {"start": v(-75.25, 6.52) * mm, "end": v(-72.05, 6.52) * mm});
            skArc(sketch, "E372", {"start": v(-105.2, 2.91) * mm, "mid": v(-105.38, 3.1) * mm, "end": v(-105.58, 3.26) * mm});
            skLineSegment(sketch, "E373", {"start": v(126.73, 63.91) * mm, "end": v(128.32, 63.91) * mm});
            skLineSegment(sketch, "E374", {"start": v(126.73, -61.76) * mm, "end": v(128.32, -61.76) * mm});
            skSolve(sketch);
        }
        {
            var Q0;
            Q0=makeQuery(id+"F0.imprint","IMPRINT",FACE,{"disambiguationData":[TD([[makeQuery(id+"F0.imprint","IMPRINT",EDGE,{"derivedFrom":sQuery(id+"F0.wireOp",EDGE,"E4")}),-1.0]])]});
            var Q1;
            Q1=makeQuery(id+"F0.imprint","IMPRINT",FACE,{"disambiguationData":[TD([[makeQuery(id+"F0.imprint","IMPRINT",EDGE,{"derivedFrom":sQuery(id+"F0.wireOp",EDGE,"E40")}),1.0]])]});
            var Q2;
            Q2=makeQuery(id+"F0.imprint","IMPRINT",FACE,{"disambiguationData":[TD([[makeQuery(id+"F0.imprint","IMPRINT",EDGE,{"derivedFrom":sQuery(id+"F0.wireOp",EDGE,"E5")}),-1.0]])]});
            var Q3;
            {var subQ0=sQuery(id+"F0.wireOp",EDGE,"E170");Q3=makeQuery(id+"F0.imprint","IMPRINT",FACE,{"disambiguationData":[TD([[makeQuery(id+"F0.imprint","IMPRINT",EDGE,{"derivedFrom":subQ0}),-1.0]])]});}
            var Q4;
            {var subQ5=sQuery(id+"F0.wireOp",EDGE,"E287");Q4=makeQuery(id+"F0.imprint","IMPRINT",FACE,{"disambiguationData":[TD([[makeQuery(id+"F0.imprint","IMPRINT",EDGE,{"derivedFrom":subQ5}),-1.0]])]});}
            var Q5;
            {var subQ0=sQuery(id+"F0.wireOp",EDGE,"E68");Q5=makeQuery(id+"F0.imprint","IMPRINT",FACE,{"disambiguationData":[TD([[makeQuery(id+"F0.imprint","IMPRINT",EDGE,{"derivedFrom":subQ0}),-1.0]])]});}
            var Q6;
            {var subQ1=sQuery(id+"F0.wireOp",EDGE,"E177");Q6=makeQuery(id+"F0.imprint","IMPRINT",FACE,{"disambiguationData":[TD([[makeQuery(id+"F0.imprint","IMPRINT",EDGE,{"derivedFrom":subQ1}),1.0]])]});}
            var Q7;
            {var subQ5=sQuery(id+"F0.wireOp",EDGE,"E286");Q7=makeQuery(id+"F0.imprint","IMPRINT",FACE,{"disambiguationData":[TD([[makeQuery(id+"F0.imprint","IMPRINT",EDGE,{"derivedFrom":subQ5}),-1.0]])]});}
            var Q8;
            {var subQ0=sQuery(id+"F0.wireOp",EDGE,"E70");Q8=makeQuery(id+"F0.imprint","IMPRINT",FACE,{"disambiguationData":[TD([[makeQuery(id+"F0.imprint","IMPRINT",EDGE,{"derivedFrom":subQ0}),-1.0]])]});}
            var Q9;
            Q9=makeQuery(id+"F0.imprint","IMPRINT",FACE,{"disambiguationData":[TD([[makeQuery(id+"F0.imprint","IMPRINT",EDGE,{"derivedFrom":sQuery(id+"F0.wireOp",EDGE,"E59")}),1.0]])]});
            var Q10;
            Q10=makeQuery(id+"F0.imprint","IMPRINT",FACE,{"disambiguationData":[TD([[makeQuery(id+"F0.imprint","IMPRINT",EDGE,{"derivedFrom":sQuery(id+"F0.wireOp",EDGE,"E178")}),1.0]])]});
            var Q11;
            Q11=makeQuery(id+"F0.imprint","IMPRINT",FACE,{"disambiguationData":[TD([[makeQuery(id+"F0.imprint","IMPRINT",EDGE,{"derivedFrom":sQuery(id+"F0.wireOp",EDGE,"E171")}),1.0]])]});
            var Q12;
            {var subQ3=sQuery(id+"F0.wireOp",EDGE,"E61");Q12=makeQuery(id+"F0.imprint","IMPRINT",FACE,{"disambiguationData":[TD([[makeQuery(id+"F0.imprint","IMPRINT",EDGE,{"derivedFrom":subQ3}),-1.0]])]});}
            var Q13;
            Q13=makeQuery(id+"F0.imprint","IMPRINT",FACE,{"disambiguationData":[TD([[makeQuery(id+"F0.imprint","IMPRINT",EDGE,{"derivedFrom":sQuery(id+"F0.wireOp",EDGE,"E40")}),-1.0]])]});
            var Q14;
            {var subQ3=sQuery(id+"F0.wireOp",EDGE,"E42");Q14=makeQuery(id+"F0.imprint","IMPRINT",FACE,{"disambiguationData":[TD([[makeQuery(id+"F0.imprint","IMPRINT",EDGE,{"derivedFrom":subQ3}),-1.0]])]});}
            var Q15;
            {var subQ1=sQuery(id+"F0.wireOp",EDGE,"E170");Q15=makeQuery(id+"F0.imprint","IMPRINT",FACE,{"disambiguationData":[TD([[makeQuery(id+"F0.imprint","IMPRINT",EDGE,{"derivedFrom":subQ1}),1.0]])]});}
            var Q16;
            {var subQ5=sQuery(id+"F0.wireOp",EDGE,"E288");Q16=makeQuery(id+"F0.imprint","IMPRINT",FACE,{"disambiguationData":[TD([[makeQuery(id+"F0.imprint","IMPRINT",EDGE,{"derivedFrom":subQ5}),1.0]])]});}
            var Q17;
            {var subQ7=sQuery(id+"F0.wireOp",EDGE,"E72");Q17=makeQuery(id+"F0.imprint","IMPRINT",FACE,{"disambiguationData":[TD([[makeQuery(id+"F0.imprint","IMPRINT",EDGE,{"derivedFrom":subQ7}),-1.0]])]});}
            var Q18;
            {var subQ5=sQuery(id+"F0.wireOp",EDGE,"E285");Q18=makeQuery(id+"F0.imprint","IMPRINT",FACE,{"disambiguationData":[TD([[makeQuery(id+"F0.imprint","IMPRINT",EDGE,{"derivedFrom":subQ5}),1.0]])]});}
            var Q19;
            {var subQ4=sQuery(id+"F0.wireOp",EDGE,"E208");Q19=makeQuery(id+"F0.imprint","IMPRINT",FACE,{"disambiguationData":[TD([[makeQuery(id+"F0.imprint","IMPRINT",EDGE,{"derivedFrom":subQ4}),1.0]])]});}
            var Q20;
            Q20=makeQuery(id+"F0.imprint","IMPRINT",FACE,{"disambiguationData":[TD([[makeQuery(id+"F0.imprint","IMPRINT",EDGE,{"derivedFrom":sQuery(id+"F0.wireOp",EDGE,"E223")}),-1.0]])]});
            var Q21;
            {var subQ3=sQuery(id+"F0.wireOp",EDGE,"E214");Q21=makeQuery(id+"F0.imprint","IMPRINT",FACE,{"disambiguationData":[TD([[makeQuery(id+"F0.imprint","IMPRINT",EDGE,{"derivedFrom":subQ3}),1.0]])]});}
            var Q22;
            {var subQ1=sQuery(id+"F0.wireOp",EDGE,"E215");Q22=makeQuery(id+"F0.imprint","IMPRINT",FACE,{"disambiguationData":[TD([[makeQuery(id+"F0.imprint","IMPRINT",EDGE,{"derivedFrom":subQ1}),1.0]])]});}
            var Q23;
            Q23=makeQuery(id+"F0.imprint","IMPRINT",FACE,{"disambiguationData":[TD([[makeQuery(id+"F0.imprint","IMPRINT",EDGE,{"derivedFrom":sQuery(id+"F0.wireOp",EDGE,"E213")}),1.0]])]});
            var Q24;
            {var subQ2=sQuery(id+"F0.wireOp",EDGE,"E210");Q24=makeQuery(id+"F0.imprint","IMPRINT",FACE,{"disambiguationData":[TD([[makeQuery(id+"F0.imprint","IMPRINT",EDGE,{"derivedFrom":subQ2}),1.0]])]});}
            var Q25;
            {var subQ0=sQuery(id+"F0.wireOp",EDGE,"E65");Q25=makeQuery(id+"F0.imprint","IMPRINT",FACE,{"disambiguationData":[TD([[makeQuery(id+"F0.imprint","IMPRINT",EDGE,{"derivedFrom":subQ0}),-1.0]])]});}
            var Q26;
            {var subQ0=sQuery(id+"F0.wireOp",EDGE,"E69");Q26=makeQuery(id+"F0.imprint","IMPRINT",FACE,{"disambiguationData":[TD([[makeQuery(id+"F0.imprint","IMPRINT",EDGE,{"derivedFrom":subQ0}),-1.0]])]});}
            var Q27;
            {var subQ0=sQuery(id+"F0.wireOp",EDGE,"E63");Q27=makeQuery(id+"F0.imprint","IMPRINT",FACE,{"disambiguationData":[TD([[makeQuery(id+"F0.imprint","IMPRINT",EDGE,{"derivedFrom":subQ0}),-1.0]])]});}
            var Q28;
            {var subQ0=sQuery(id+"F0.wireOp",EDGE,"E64");Q28=makeQuery(id+"F0.imprint","IMPRINT",FACE,{"disambiguationData":[TD([[makeQuery(id+"F0.imprint","IMPRINT",EDGE,{"derivedFrom":subQ0}),-1.0]])]});}
            var Q29;
            {var subQ0=sQuery(id+"F0.wireOp",EDGE,"E22");Q29=makeQuery(id+"F0.imprint","IMPRINT",FACE,{"disambiguationData":[TD([[makeQuery(id+"F0.imprint","IMPRINT",EDGE,{"derivedFrom":subQ0}),-1.0]])]});}
            var Q30;
            {var subQ0=sQuery(id+"F0.wireOp",EDGE,"E67");Q30=makeQuery(id+"F0.imprint","IMPRINT",FACE,{"disambiguationData":[TD([[makeQuery(id+"F0.imprint","IMPRINT",EDGE,{"derivedFrom":subQ0}),-1.0]])]});}
            var Q31;
            {var subQ7=sQuery(id+"F0.wireOp",EDGE,"E177");Q31=makeQuery(id+"F0.imprint","IMPRINT",FACE,{"disambiguationData":[TD([[makeQuery(id+"F0.imprint","IMPRINT",EDGE,{"derivedFrom":subQ7}),-1.0]])]});}
            var Q32;
            {var subQ0=sQuery(id+"F0.wireOp",EDGE,"E71");Q32=makeQuery(id+"F0.imprint","IMPRINT",FACE,{"disambiguationData":[TD([[makeQuery(id+"F0.imprint","IMPRINT",EDGE,{"derivedFrom":subQ0}),-1.0]])]});}
            var Q33;
            {var subQ0=sQuery(id+"F0.wireOp",EDGE,"E66");Q33=makeQuery(id+"F0.imprint","IMPRINT",FACE,{"disambiguationData":[TD([[makeQuery(id+"F0.imprint","IMPRINT",EDGE,{"derivedFrom":subQ0}),-1.0]])]});}
            var Q34;
            {var subQ0=sQuery(id+"F0.wireOp",EDGE,"E62");Q34=makeQuery(id+"F0.imprint","IMPRINT",FACE,{"disambiguationData":[TD([[makeQuery(id+"F0.imprint","IMPRINT",EDGE,{"derivedFrom":subQ0}),-1.0]])]});}
            var Q35;
            {var subQ0=sQuery(id+"F0.wireOp",EDGE,"E22");Q35=makeQuery(id+"F0.imprint","IMPRINT",FACE,{"disambiguationData":[TD([[makeQuery(id+"F0.imprint","IMPRINT",EDGE,{"derivedFrom":subQ0}),1.0]])]});}
            var Q36;
            Q36=makeQuery(id+"F0.imprint","IMPRINT",FACE,{"disambiguationData":[TD([[makeQuery(id+"F0.imprint","IMPRINT",EDGE,{"derivedFrom":sQuery(id+"F0.wireOp",EDGE,"E155")}),-1.0]])]});
            var Q37;
            Q37=makeQuery(id+"F0.imprint","IMPRINT",FACE,{"disambiguationData":[TD([[makeQuery(id+"F0.imprint","IMPRINT",EDGE,{"derivedFrom":sQuery(id+"F0.wireOp",EDGE,"E157")}),-1.0]])]});
            var Q38;
            Q38=makeQuery(id+"F0.imprint","IMPRINT",FACE,{"disambiguationData":[TD([[makeQuery(id+"F0.imprint","IMPRINT",EDGE,{"derivedFrom":sQuery(id+"F0.wireOp",EDGE,"E156")}),-1.0]])]});
            var Q39;
            Q39=makeQuery(id+"F0.imprint","IMPRINT",FACE,{"disambiguationData":[TD([[makeQuery(id+"F0.imprint","IMPRINT",EDGE,{"derivedFrom":sQuery(id+"F0.wireOp",EDGE,"E154")}),-1.0]])]});
            var Q40;
            Q40=makeQuery(id+"F0.imprint","IMPRINT",FACE,{"disambiguationData":[TD([[makeQuery(id+"F0.imprint","IMPRINT",EDGE,{"derivedFrom":sQuery(id+"F0.wireOp",EDGE,"E153")}),-1.0]])]});
            var Q41;
            {var subQ0=sQuery(id+"F0.wireOp",EDGE,"E366");Q41=makeQuery(id+"F0.imprint","IMPRINT",FACE,{"disambiguationData":[TD([[makeQuery(id+"F0.imprint","IMPRINT",EDGE,{"derivedFrom":subQ0}),1.0]])]});}
            var Q42;
            {var subQ0=sQuery(id+"F0.wireOp",EDGE,"E365");Q42=makeQuery(id+"F0.imprint","IMPRINT",FACE,{"disambiguationData":[TD([[makeQuery(id+"F0.imprint","IMPRINT",EDGE,{"derivedFrom":subQ0}),-1.0]])]});}
            var Q43;
            {var subQ0=sQuery(id+"F0.wireOp",EDGE,"E369");Q43=makeQuery(id+"F0.imprint","IMPRINT",FACE,{"disambiguationData":[TD([[makeQuery(id+"F0.imprint","IMPRINT",EDGE,{"derivedFrom":subQ0}),1.0]])]});}
            var Q44;
            {var subQ0=sQuery(id+"F0.wireOp",EDGE,"E368");Q44=makeQuery(id+"F0.imprint","IMPRINT",FACE,{"disambiguationData":[TD([[makeQuery(id+"F0.imprint","IMPRINT",EDGE,{"derivedFrom":subQ0}),1.0]])]});}
            var Q45;
            {var subQ1=sQuery(id+"F0.wireOp",EDGE,"E353");Q45=makeQuery(id+"F0.imprint","IMPRINT",FACE,{"disambiguationData":[TD([[makeQuery(id+"F0.imprint","IMPRINT",EDGE,{"derivedFrom":subQ1}),1.0]])]});}
            var Q46;
            {var subQ0=sQuery(id+"F0.wireOp",EDGE,"E367");Q46=makeQuery(id+"F0.imprint","IMPRINT",FACE,{"disambiguationData":[TD([[makeQuery(id+"F0.imprint","IMPRINT",EDGE,{"derivedFrom":subQ0}),-1.0]])]});}
            var Q47;
            {var subQ9=sQuery(id+"F0.wireOp",EDGE,"E159");Q47=makeQuery(id+"F0.imprint","IMPRINT",FACE,{"disambiguationData":[TD([[makeQuery(id+"F0.imprint","IMPRINT",EDGE,{"derivedFrom":subQ9}),1.0]])]});}
            var Q48;
            {var subQ9=sQuery(id+"F0.wireOp",EDGE,"E353");Q48=makeQuery(id+"F0.imprint","IMPRINT",FACE,{"disambiguationData":[TD([[makeQuery(id+"F0.imprint","IMPRINT",EDGE,{"derivedFrom":subQ9}),-1.0]])]});}
            var Q49;
            {var subQ2=sQuery(id+"F0.wireOp",EDGE,"E160");Q49=makeQuery(id+"F0.imprint","IMPRINT",FACE,{"disambiguationData":[TD([[makeQuery(id+"F0.imprint","IMPRINT",EDGE,{"derivedFrom":subQ2}),-1.0]])]});}
            var Q50;
            {var subQ2=sQuery(id+"F0.wireOp",EDGE,"E358");Q50=makeQuery(id+"F0.imprint","IMPRINT",FACE,{"disambiguationData":[TD([[makeQuery(id+"F0.imprint","IMPRINT",EDGE,{"derivedFrom":subQ2}),-1.0]])]});}
            var Q51;
            {var subQ2=sQuery(id+"F0.wireOp",EDGE,"E356");Q51=makeQuery(id+"F0.imprint","IMPRINT",FACE,{"disambiguationData":[TD([[makeQuery(id+"F0.imprint","IMPRINT",EDGE,{"derivedFrom":subQ2}),-1.0]])]});}
            var Q52;
            {var subQ2=sQuery(id+"F0.wireOp",EDGE,"E134");Q52=makeQuery(id+"F0.imprint","IMPRINT",FACE,{"disambiguationData":[TD([[makeQuery(id+"F0.imprint","IMPRINT",EDGE,{"derivedFrom":subQ2}),-1.0]])]});}
            var Q53;
            {var subQ0=sQuery(id+"F0.wireOp",EDGE,"E152");Q53=makeQuery(id+"F0.imprint","IMPRINT",FACE,{"disambiguationData":[TD([[makeQuery(id+"F0.imprint","IMPRINT",EDGE,{"derivedFrom":subQ0}),1.0]])]});}
            var Q54;
            {var subQ3=sQuery(id+"F0.wireOp",EDGE,"E128");Q54=makeQuery(id+"F0.imprint","IMPRINT",FACE,{"disambiguationData":[TD([[makeQuery(id+"F0.imprint","IMPRINT",EDGE,{"derivedFrom":subQ3}),1.0]])]});}
            var Q55;
            {var subQ2=sQuery(id+"F0.wireOp",EDGE,"E152");Q55=makeQuery(id+"F0.imprint","IMPRINT",FACE,{"disambiguationData":[TD([[makeQuery(id+"F0.imprint","IMPRINT",EDGE,{"derivedFrom":subQ2}),-1.0]])]});}
            var Q56;
            Q56=makeQuery(id+"F0.imprint","IMPRINT",FACE,{"disambiguationData":[TD([[makeQuery(id+"F0.imprint","IMPRINT",EDGE,{"derivedFrom":sQuery(id+"F0.wireOp",EDGE,"E113")}),-1.0]])]});
            var Q57;
            {var subQ0=sQuery(id+"F0.wireOp",EDGE,"E149");Q57=makeQuery(id+"F0.imprint","IMPRINT",FACE,{"disambiguationData":[TD([[makeQuery(id+"F0.imprint","IMPRINT",EDGE,{"derivedFrom":subQ0}),1.0]])]});}
            var Q58;
            {var subQ4=sQuery(id+"F0.wireOp",EDGE,"E98");Q58=makeQuery(id+"F0.imprint","IMPRINT",FACE,{"disambiguationData":[TD([[makeQuery(id+"F0.imprint","IMPRINT",EDGE,{"derivedFrom":subQ4}),1.0]])]});}
            var Q59;
            {var subQ2=sQuery(id+"F0.wireOp",EDGE,"E149");Q59=makeQuery(id+"F0.imprint","IMPRINT",FACE,{"disambiguationData":[TD([[makeQuery(id+"F0.imprint","IMPRINT",EDGE,{"derivedFrom":subQ2}),-1.0]])]});}
            var Q60;
            {var subQ4=sQuery(id+"F0.wireOp",EDGE,"E96");Q60=makeQuery(id+"F0.imprint","IMPRINT",FACE,{"disambiguationData":[TD([[makeQuery(id+"F0.imprint","IMPRINT",EDGE,{"derivedFrom":subQ4}),1.0]])]});}
            var Q61;
            {var subQ0=sQuery(id+"F0.wireOp",EDGE,"E137");Q61=makeQuery(id+"F0.imprint","IMPRINT",FACE,{"disambiguationData":[TD([[makeQuery(id+"F0.imprint","IMPRINT",EDGE,{"derivedFrom":subQ0}),1.0]])]});}
            var Q62;
            {var subQ1=sQuery(id+"F0.wireOp",EDGE,"E97");Q62=makeQuery(id+"F0.imprint","IMPRINT",FACE,{"disambiguationData":[TD([[makeQuery(id+"F0.imprint","IMPRINT",EDGE,{"derivedFrom":subQ1}),1.0]])]});}
            var Q63;
            {var subQ0=sQuery(id+"F0.wireOp",EDGE,"E146");Q63=makeQuery(id+"F0.imprint","IMPRINT",FACE,{"disambiguationData":[TD([[makeQuery(id+"F0.imprint","IMPRINT",EDGE,{"derivedFrom":subQ0}),1.0]])]});}
            var Q64;
            {var subQ3=sQuery(id+"F0.wireOp",EDGE,"E94");Q64=makeQuery(id+"F0.imprint","IMPRINT",FACE,{"disambiguationData":[TD([[makeQuery(id+"F0.imprint","IMPRINT",EDGE,{"derivedFrom":subQ3}),1.0]])]});}
            var Q65;
            {var subQ1=sQuery(id+"F0.wireOp",EDGE,"E95");Q65=makeQuery(id+"F0.imprint","IMPRINT",FACE,{"disambiguationData":[TD([[makeQuery(id+"F0.imprint","IMPRINT",EDGE,{"derivedFrom":subQ1}),1.0]])]});}
            var Q66;
            {var subQ2=sQuery(id+"F0.wireOp",EDGE,"E146");Q66=makeQuery(id+"F0.imprint","IMPRINT",FACE,{"disambiguationData":[TD([[makeQuery(id+"F0.imprint","IMPRINT",EDGE,{"derivedFrom":subQ2}),-1.0]])]});}
            var Q67;
            {var subQ5=sQuery(id+"F0.wireOp",EDGE,"E92");Q67=makeQuery(id+"F0.imprint","IMPRINT",FACE,{"disambiguationData":[TD([[makeQuery(id+"F0.imprint","IMPRINT",EDGE,{"derivedFrom":subQ5}),1.0]])]});}
            var Q68;
            {var subQ1=sQuery(id+"F0.wireOp",EDGE,"E86");Q68=makeQuery(id+"F0.imprint","IMPRINT",FACE,{"disambiguationData":[TD([[makeQuery(id+"F0.imprint","IMPRINT",EDGE,{"derivedFrom":subQ1}),1.0]])]});}
            var Q69;
            {var subQ1=sQuery(id+"F0.wireOp",EDGE,"E91");Q69=makeQuery(id+"F0.imprint","IMPRINT",FACE,{"disambiguationData":[TD([[makeQuery(id+"F0.imprint","IMPRINT",EDGE,{"derivedFrom":subQ1}),1.0]])]});}
            var Q70;
            {var subQ2=sQuery(id+"F0.wireOp",EDGE,"E143");Q70=makeQuery(id+"F0.imprint","IMPRINT",FACE,{"disambiguationData":[TD([[makeQuery(id+"F0.imprint","IMPRINT",EDGE,{"derivedFrom":subQ2}),-1.0]])]});}
            var Q71;
            {var subQ6=sQuery(id+"F0.wireOp",EDGE,"E88");Q71=makeQuery(id+"F0.imprint","IMPRINT",FACE,{"disambiguationData":[TD([[makeQuery(id+"F0.imprint","IMPRINT",EDGE,{"derivedFrom":subQ6}),1.0]])]});}
            var Q72;
            {var subQ2=sQuery(id+"F0.wireOp",EDGE,"E89");Q72=makeQuery(id+"F0.imprint","IMPRINT",FACE,{"disambiguationData":[TD([[makeQuery(id+"F0.imprint","IMPRINT",EDGE,{"derivedFrom":subQ2}),1.0]])]});}
            var Q73;
            {var subQ0=sQuery(id+"F0.wireOp",EDGE,"E140");Q73=makeQuery(id+"F0.imprint","IMPRINT",FACE,{"disambiguationData":[TD([[makeQuery(id+"F0.imprint","IMPRINT",EDGE,{"derivedFrom":subQ0}),1.0]])]});}
            var Q74;
            {var subQ2=sQuery(id+"F0.wireOp",EDGE,"E140");Q74=makeQuery(id+"F0.imprint","IMPRINT",FACE,{"disambiguationData":[TD([[makeQuery(id+"F0.imprint","IMPRINT",EDGE,{"derivedFrom":subQ2}),-1.0]])]});}
            var Q75;
            {var subQ1=sQuery(id+"F0.wireOp",EDGE,"E93");Q75=makeQuery(id+"F0.imprint","IMPRINT",FACE,{"disambiguationData":[TD([[makeQuery(id+"F0.imprint","IMPRINT",EDGE,{"derivedFrom":subQ1}),1.0]])]});}
            var Q76;
            {var subQ0=sQuery(id+"F0.wireOp",EDGE,"E143");Q76=makeQuery(id+"F0.imprint","IMPRINT",FACE,{"disambiguationData":[TD([[makeQuery(id+"F0.imprint","IMPRINT",EDGE,{"derivedFrom":subQ0}),1.0]])]});}
            var Q77;
            {var subQ3=sQuery(id+"F0.wireOp",EDGE,"E90");Q77=makeQuery(id+"F0.imprint","IMPRINT",FACE,{"disambiguationData":[TD([[makeQuery(id+"F0.imprint","IMPRINT",EDGE,{"derivedFrom":subQ3}),1.0]])]});}
            var Q78;
            {var subQ1=sQuery(id+"F0.wireOp",EDGE,"E87");Q78=makeQuery(id+"F0.imprint","IMPRINT",FACE,{"disambiguationData":[TD([[makeQuery(id+"F0.imprint","IMPRINT",EDGE,{"derivedFrom":subQ1}),1.0]])]});}
            var Q79;
            {var subQ2=sQuery(id+"F0.wireOp",EDGE,"E137");Q79=makeQuery(id+"F0.imprint","IMPRINT",FACE,{"disambiguationData":[TD([[makeQuery(id+"F0.imprint","IMPRINT",EDGE,{"derivedFrom":subQ2}),-1.0]])]});}
            var Q80;
            {var subQ0=sQuery(id+"F0.wireOp",EDGE,"E134");Q80=makeQuery(id+"F0.imprint","IMPRINT",FACE,{"disambiguationData":[TD([[makeQuery(id+"F0.imprint","IMPRINT",EDGE,{"derivedFrom":subQ0}),1.0]])]});}
            var Q81;
            Q81=makeQuery(id+"F0.imprint","IMPRINT",FACE,{"disambiguationData":[TD([[makeQuery(id+"F0.imprint","IMPRINT",EDGE,{"derivedFrom":sQuery(id+"F0.wireOp",EDGE,"E163")}),-1.0]])]});
            var Q82;
            Q82=makeQuery(id+"F0.imprint","IMPRINT",FACE,{"disambiguationData":[TD([[makeQuery(id+"F0.imprint","IMPRINT",EDGE,{"derivedFrom":sQuery(id+"F0.wireOp",EDGE,"E164")}),1.0]])]});
            var Q83;
            {var subQ0=sQuery(id+"F0.wireOp",EDGE,"E29");Q83=makeQuery(id+"F0.imprint","IMPRINT",FACE,{"disambiguationData":[TD([[makeQuery(id+"F0.imprint","IMPRINT",EDGE,{"derivedFrom":subQ0}),-1.0]])]});}
            var Q84;
            {var subQ0=sQuery(id+"F0.wireOp",EDGE,"E26");Q84=makeQuery(id+"F0.imprint","IMPRINT",FACE,{"disambiguationData":[TD([[makeQuery(id+"F0.imprint","IMPRINT",EDGE,{"derivedFrom":subQ0}),-1.0]])]});}
            var Q85;
            {var subQ0=sQuery(id+"F0.wireOp",EDGE,"E38");Q85=makeQuery(id+"F0.imprint","IMPRINT",FACE,{"disambiguationData":[TD([[makeQuery(id+"F0.imprint","IMPRINT",EDGE,{"derivedFrom":subQ0}),-1.0]])]});}
            var Q86;
            {var subQ0=sQuery(id+"F0.wireOp",EDGE,"E38");Q86=makeQuery(id+"F0.imprint","IMPRINT",FACE,{"disambiguationData":[TD([[makeQuery(id+"F0.imprint","IMPRINT",EDGE,{"derivedFrom":subQ0}),1.0]])]});}
            var Q87;
            {var subQ0=sQuery(id+"F0.wireOp",EDGE,"E35");Q87=makeQuery(id+"F0.imprint","IMPRINT",FACE,{"disambiguationData":[TD([[makeQuery(id+"F0.imprint","IMPRINT",EDGE,{"derivedFrom":subQ0}),-1.0]])]});}
            var Q88;
            {var subQ0=sQuery(id+"F0.wireOp",EDGE,"E29");Q88=makeQuery(id+"F0.imprint","IMPRINT",FACE,{"disambiguationData":[TD([[makeQuery(id+"F0.imprint","IMPRINT",EDGE,{"derivedFrom":subQ0}),1.0]])]});}
            var Q89;
            {var subQ0=sQuery(id+"F0.wireOp",EDGE,"E32");Q89=makeQuery(id+"F0.imprint","IMPRINT",FACE,{"disambiguationData":[TD([[makeQuery(id+"F0.imprint","IMPRINT",EDGE,{"derivedFrom":subQ0}),1.0]])]});}
            var Q90;
            {var subQ0=sQuery(id+"F0.wireOp",EDGE,"E35");Q90=makeQuery(id+"F0.imprint","IMPRINT",FACE,{"disambiguationData":[TD([[makeQuery(id+"F0.imprint","IMPRINT",EDGE,{"derivedFrom":subQ0}),1.0]])]});}
            var Q91;
            {var subQ0=sQuery(id+"F0.wireOp",EDGE,"E32");Q91=makeQuery(id+"F0.imprint","IMPRINT",FACE,{"disambiguationData":[TD([[makeQuery(id+"F0.imprint","IMPRINT",EDGE,{"derivedFrom":subQ0}),-1.0]])]});}
            var Q92;
            {var subQ0=sQuery(id+"F0.wireOp",EDGE,"E26");Q92=makeQuery(id+"F0.imprint","IMPRINT",FACE,{"disambiguationData":[TD([[makeQuery(id+"F0.imprint","IMPRINT",EDGE,{"derivedFrom":subQ0}),1.0]])]});}
            var Q93;
            {var subQ0=sQuery(id+"F0.wireOp",EDGE,"E23");Q93=makeQuery(id+"F0.imprint","IMPRINT",FACE,{"disambiguationData":[TD([[makeQuery(id+"F0.imprint","IMPRINT",EDGE,{"derivedFrom":subQ0}),-1.0]])]});}
            extrude(context, id + "F1", {"entities" : qUnion([Q0, Q1, Q2, Q3, Q4, Q5, Q6, Q7, Q8, Q9, Q10, Q11, Q12, Q13, Q14, Q15, Q16, Q17, Q18, Q19, Q20, Q21, Q22, Q23, Q24, Q25, Q26, Q27, Q28, Q29, Q30, Q31, Q32, Q33, Q34, Q35, Q36, Q37, Q38, Q39, Q40, Q41, Q42, Q43, Q44, Q45, Q46, Q47, Q48, Q49, Q50, Q51, Q52, Q53, Q54, Q55, Q56, Q57, Q58, Q59, Q60, Q61, Q62, Q63, Q64, Q65, Q66, Q67, Q68, Q69, Q70, Q71, Q72, Q73, Q74, Q75, Q76, Q77, Q78, Q79, Q80, Q81, Q82, Q83, Q84, Q85, Q86, Q87, Q88, Q89, Q90, Q91, Q92, Q93]), "depth" : 1.6 * mm});
        }
        {
            var Q0;
            Q0=makeQuery(id+"F0.imprint","IMPRINT",FACE,{"disambiguationData":[TD([[makeQuery(id+"F0.imprint","IMPRINT",EDGE,{"derivedFrom":sQuery(id+"F0.wireOp",EDGE,"E40")}),1.0]])]});
            var Q1;
            {var subQ2=sQuery(id+"F0.wireOp",EDGE,"E160");Q1=makeQuery(id+"F0.imprint","IMPRINT",FACE,{"disambiguationData":[TD([[makeQuery(id+"F0.imprint","IMPRINT",EDGE,{"derivedFrom":subQ2}),-1.0]])]});}
            var Q2;
            {var subQ9=sQuery(id+"F0.wireOp",EDGE,"E353");Q2=makeQuery(id+"F0.imprint","IMPRINT",FACE,{"disambiguationData":[TD([[makeQuery(id+"F0.imprint","IMPRINT",EDGE,{"derivedFrom":subQ9}),-1.0]])]});}
            var Q3;
            {var subQ9=sQuery(id+"F0.wireOp",EDGE,"E159");Q3=makeQuery(id+"F0.imprint","IMPRINT",FACE,{"disambiguationData":[TD([[makeQuery(id+"F0.imprint","IMPRINT",EDGE,{"derivedFrom":subQ9}),1.0]])]});}
            var Q4;
            {var subQ0=sQuery(id+"F0.wireOp",EDGE,"E367");Q4=makeQuery(id+"F0.imprint","IMPRINT",FACE,{"disambiguationData":[TD([[makeQuery(id+"F0.imprint","IMPRINT",EDGE,{"derivedFrom":subQ0}),-1.0]])]});}
            var Q5;
            Q5=makeQuery(id+"F0.imprint","IMPRINT",FACE,{"disambiguationData":[TD([[makeQuery(id+"F0.imprint","IMPRINT",EDGE,{"derivedFrom":sQuery(id+"F0.wireOp",EDGE,"E153")}),-1.0]])]});
            var Q6;
            Q6=makeQuery(id+"F0.imprint","IMPRINT",FACE,{"disambiguationData":[TD([[makeQuery(id+"F0.imprint","IMPRINT",EDGE,{"derivedFrom":sQuery(id+"F0.wireOp",EDGE,"E154")}),-1.0]])]});
            var Q7;
            Q7=makeQuery(id+"F0.imprint","IMPRINT",FACE,{"disambiguationData":[TD([[makeQuery(id+"F0.imprint","IMPRINT",EDGE,{"derivedFrom":sQuery(id+"F0.wireOp",EDGE,"E156")}),-1.0]])]});
            var Q8;
            Q8=makeQuery(id+"F0.imprint","IMPRINT",FACE,{"disambiguationData":[TD([[makeQuery(id+"F0.imprint","IMPRINT",EDGE,{"derivedFrom":sQuery(id+"F0.wireOp",EDGE,"E157")}),-1.0]])]});
            var Q9;
            Q9=makeQuery(id+"F0.imprint","IMPRINT",FACE,{"disambiguationData":[TD([[makeQuery(id+"F0.imprint","IMPRINT",EDGE,{"derivedFrom":sQuery(id+"F0.wireOp",EDGE,"E155")}),-1.0]])]});
            var Q10;
            {var subQ0=sQuery(id+"F0.wireOp",EDGE,"E368");Q10=makeQuery(id+"F0.imprint","IMPRINT",FACE,{"disambiguationData":[TD([[makeQuery(id+"F0.imprint","IMPRINT",EDGE,{"derivedFrom":subQ0}),1.0]])]});}
            var Q11;
            {var subQ0=sQuery(id+"F0.wireOp",EDGE,"E369");Q11=makeQuery(id+"F0.imprint","IMPRINT",FACE,{"disambiguationData":[TD([[makeQuery(id+"F0.imprint","IMPRINT",EDGE,{"derivedFrom":subQ0}),1.0]])]});}
            var Q12;
            {var subQ0=sQuery(id+"F0.wireOp",EDGE,"E365");Q12=makeQuery(id+"F0.imprint","IMPRINT",FACE,{"disambiguationData":[TD([[makeQuery(id+"F0.imprint","IMPRINT",EDGE,{"derivedFrom":subQ0}),-1.0]])]});}
            var Q13;
            {var subQ0=sQuery(id+"F0.wireOp",EDGE,"E366");Q13=makeQuery(id+"F0.imprint","IMPRINT",FACE,{"disambiguationData":[TD([[makeQuery(id+"F0.imprint","IMPRINT",EDGE,{"derivedFrom":subQ0}),1.0]])]});}
            var Q14;
            {var subQ1=sQuery(id+"F0.wireOp",EDGE,"E353");Q14=makeQuery(id+"F0.imprint","IMPRINT",FACE,{"disambiguationData":[TD([[makeQuery(id+"F0.imprint","IMPRINT",EDGE,{"derivedFrom":subQ1}),1.0]])]});}
            var Q15;
            {var subQ2=sQuery(id+"F0.wireOp",EDGE,"E356");Q15=makeQuery(id+"F0.imprint","IMPRINT",FACE,{"disambiguationData":[TD([[makeQuery(id+"F0.imprint","IMPRINT",EDGE,{"derivedFrom":subQ2}),-1.0]])]});}
            var Q16;
            {var subQ2=sQuery(id+"F0.wireOp",EDGE,"E358");Q16=makeQuery(id+"F0.imprint","IMPRINT",FACE,{"disambiguationData":[TD([[makeQuery(id+"F0.imprint","IMPRINT",EDGE,{"derivedFrom":subQ2}),-1.0]])]});}
            var Q17;
            {var subQ1=sQuery(id+"F0.wireOp",EDGE,"E93");Q17=makeQuery(id+"F0.imprint","IMPRINT",FACE,{"disambiguationData":[TD([[makeQuery(id+"F0.imprint","IMPRINT",EDGE,{"derivedFrom":subQ1}),1.0]])]});}
            var Q18;
            {var subQ0=sQuery(id+"F0.wireOp",EDGE,"E143");Q18=makeQuery(id+"F0.imprint","IMPRINT",FACE,{"disambiguationData":[TD([[makeQuery(id+"F0.imprint","IMPRINT",EDGE,{"derivedFrom":subQ0}),1.0]])]});}
            var Q19;
            {var subQ3=sQuery(id+"F0.wireOp",EDGE,"E90");Q19=makeQuery(id+"F0.imprint","IMPRINT",FACE,{"disambiguationData":[TD([[makeQuery(id+"F0.imprint","IMPRINT",EDGE,{"derivedFrom":subQ3}),1.0]])]});}
            var Q20;
            {var subQ1=sQuery(id+"F0.wireOp",EDGE,"E86");Q20=makeQuery(id+"F0.imprint","IMPRINT",FACE,{"disambiguationData":[TD([[makeQuery(id+"F0.imprint","IMPRINT",EDGE,{"derivedFrom":subQ1}),1.0]])]});}
            var Q21;
            {var subQ2=sQuery(id+"F0.wireOp",EDGE,"E140");Q21=makeQuery(id+"F0.imprint","IMPRINT",FACE,{"disambiguationData":[TD([[makeQuery(id+"F0.imprint","IMPRINT",EDGE,{"derivedFrom":subQ2}),-1.0]])]});}
            var Q22;
            {var subQ0=sQuery(id+"F0.wireOp",EDGE,"E137");Q22=makeQuery(id+"F0.imprint","IMPRINT",FACE,{"disambiguationData":[TD([[makeQuery(id+"F0.imprint","IMPRINT",EDGE,{"derivedFrom":subQ0}),1.0]])]});}
            var Q23;
            {var subQ2=sQuery(id+"F0.wireOp",EDGE,"E137");Q23=makeQuery(id+"F0.imprint","IMPRINT",FACE,{"disambiguationData":[TD([[makeQuery(id+"F0.imprint","IMPRINT",EDGE,{"derivedFrom":subQ2}),-1.0]])]});}
            var Q24;
            {var subQ0=sQuery(id+"F0.wireOp",EDGE,"E140");Q24=makeQuery(id+"F0.imprint","IMPRINT",FACE,{"disambiguationData":[TD([[makeQuery(id+"F0.imprint","IMPRINT",EDGE,{"derivedFrom":subQ0}),1.0]])]});}
            var Q25;
            {var subQ2=sQuery(id+"F0.wireOp",EDGE,"E89");Q25=makeQuery(id+"F0.imprint","IMPRINT",FACE,{"disambiguationData":[TD([[makeQuery(id+"F0.imprint","IMPRINT",EDGE,{"derivedFrom":subQ2}),1.0]])]});}
            var Q26;
            {var subQ6=sQuery(id+"F0.wireOp",EDGE,"E88");Q26=makeQuery(id+"F0.imprint","IMPRINT",FACE,{"disambiguationData":[TD([[makeQuery(id+"F0.imprint","IMPRINT",EDGE,{"derivedFrom":subQ6}),1.0]])]});}
            var Q27;
            {var subQ2=sQuery(id+"F0.wireOp",EDGE,"E143");Q27=makeQuery(id+"F0.imprint","IMPRINT",FACE,{"disambiguationData":[TD([[makeQuery(id+"F0.imprint","IMPRINT",EDGE,{"derivedFrom":subQ2}),-1.0]])]});}
            var Q28;
            {var subQ1=sQuery(id+"F0.wireOp",EDGE,"E91");Q28=makeQuery(id+"F0.imprint","IMPRINT",FACE,{"disambiguationData":[TD([[makeQuery(id+"F0.imprint","IMPRINT",EDGE,{"derivedFrom":subQ1}),1.0]])]});}
            var Q29;
            {var subQ5=sQuery(id+"F0.wireOp",EDGE,"E92");Q29=makeQuery(id+"F0.imprint","IMPRINT",FACE,{"disambiguationData":[TD([[makeQuery(id+"F0.imprint","IMPRINT",EDGE,{"derivedFrom":subQ5}),1.0]])]});}
            var Q30;
            {var subQ2=sQuery(id+"F0.wireOp",EDGE,"E146");Q30=makeQuery(id+"F0.imprint","IMPRINT",FACE,{"disambiguationData":[TD([[makeQuery(id+"F0.imprint","IMPRINT",EDGE,{"derivedFrom":subQ2}),-1.0]])]});}
            var Q31;
            {var subQ1=sQuery(id+"F0.wireOp",EDGE,"E95");Q31=makeQuery(id+"F0.imprint","IMPRINT",FACE,{"disambiguationData":[TD([[makeQuery(id+"F0.imprint","IMPRINT",EDGE,{"derivedFrom":subQ1}),1.0]])]});}
            var Q32;
            {var subQ3=sQuery(id+"F0.wireOp",EDGE,"E94");Q32=makeQuery(id+"F0.imprint","IMPRINT",FACE,{"disambiguationData":[TD([[makeQuery(id+"F0.imprint","IMPRINT",EDGE,{"derivedFrom":subQ3}),1.0]])]});}
            var Q33;
            {var subQ0=sQuery(id+"F0.wireOp",EDGE,"E146");Q33=makeQuery(id+"F0.imprint","IMPRINT",FACE,{"disambiguationData":[TD([[makeQuery(id+"F0.imprint","IMPRINT",EDGE,{"derivedFrom":subQ0}),1.0]])]});}
            var Q34;
            {var subQ1=sQuery(id+"F0.wireOp",EDGE,"E97");Q34=makeQuery(id+"F0.imprint","IMPRINT",FACE,{"disambiguationData":[TD([[makeQuery(id+"F0.imprint","IMPRINT",EDGE,{"derivedFrom":subQ1}),1.0]])]});}
            var Q35;
            {var subQ4=sQuery(id+"F0.wireOp",EDGE,"E96");Q35=makeQuery(id+"F0.imprint","IMPRINT",FACE,{"disambiguationData":[TD([[makeQuery(id+"F0.imprint","IMPRINT",EDGE,{"derivedFrom":subQ4}),1.0]])]});}
            var Q36;
            {var subQ2=sQuery(id+"F0.wireOp",EDGE,"E149");Q36=makeQuery(id+"F0.imprint","IMPRINT",FACE,{"disambiguationData":[TD([[makeQuery(id+"F0.imprint","IMPRINT",EDGE,{"derivedFrom":subQ2}),-1.0]])]});}
            var Q37;
            {var subQ4=sQuery(id+"F0.wireOp",EDGE,"E98");Q37=makeQuery(id+"F0.imprint","IMPRINT",FACE,{"disambiguationData":[TD([[makeQuery(id+"F0.imprint","IMPRINT",EDGE,{"derivedFrom":subQ4}),1.0]])]});}
            var Q38;
            {var subQ0=sQuery(id+"F0.wireOp",EDGE,"E149");Q38=makeQuery(id+"F0.imprint","IMPRINT",FACE,{"disambiguationData":[TD([[makeQuery(id+"F0.imprint","IMPRINT",EDGE,{"derivedFrom":subQ0}),1.0]])]});}
            var Q39;
            Q39=makeQuery(id+"F0.imprint","IMPRINT",FACE,{"disambiguationData":[TD([[makeQuery(id+"F0.imprint","IMPRINT",EDGE,{"derivedFrom":sQuery(id+"F0.wireOp",EDGE,"E113")}),-1.0]])]});
            var Q40;
            {var subQ2=sQuery(id+"F0.wireOp",EDGE,"E152");Q40=makeQuery(id+"F0.imprint","IMPRINT",FACE,{"disambiguationData":[TD([[makeQuery(id+"F0.imprint","IMPRINT",EDGE,{"derivedFrom":subQ2}),-1.0]])]});}
            var Q41;
            {var subQ3=sQuery(id+"F0.wireOp",EDGE,"E128");Q41=makeQuery(id+"F0.imprint","IMPRINT",FACE,{"disambiguationData":[TD([[makeQuery(id+"F0.imprint","IMPRINT",EDGE,{"derivedFrom":subQ3}),1.0]])]});}
            var Q42;
            {var subQ0=sQuery(id+"F0.wireOp",EDGE,"E152");Q42=makeQuery(id+"F0.imprint","IMPRINT",FACE,{"disambiguationData":[TD([[makeQuery(id+"F0.imprint","IMPRINT",EDGE,{"derivedFrom":subQ0}),1.0]])]});}
            var Q43;
            {var subQ2=sQuery(id+"F0.wireOp",EDGE,"E134");Q43=makeQuery(id+"F0.imprint","IMPRINT",FACE,{"disambiguationData":[TD([[makeQuery(id+"F0.imprint","IMPRINT",EDGE,{"derivedFrom":subQ2}),-1.0]])]});}
            var Q44;
            {var subQ0=sQuery(id+"F0.wireOp",EDGE,"E134");Q44=makeQuery(id+"F0.imprint","IMPRINT",FACE,{"disambiguationData":[TD([[makeQuery(id+"F0.imprint","IMPRINT",EDGE,{"derivedFrom":subQ0}),1.0]])]});}
            var Q45;
            {var subQ1=sQuery(id+"F0.wireOp",EDGE,"E87");Q45=makeQuery(id+"F0.imprint","IMPRINT",FACE,{"disambiguationData":[TD([[makeQuery(id+"F0.imprint","IMPRINT",EDGE,{"derivedFrom":subQ1}),1.0]])]});}
            var Q46;
            Q46=makeQuery(id+"F0.imprint","IMPRINT",FACE,{"disambiguationData":[TD([[makeQuery(id+"F0.imprint","IMPRINT",EDGE,{"derivedFrom":sQuery(id+"F0.wireOp",EDGE,"E163")}),-1.0]])]});
            var Q47;
            Q47=makeQuery(id+"F0.imprint","IMPRINT",FACE,{"disambiguationData":[TD([[makeQuery(id+"F0.imprint","IMPRINT",EDGE,{"derivedFrom":sQuery(id+"F0.wireOp",EDGE,"E164")}),1.0]])]});
            var Q48;
            {var subQ0=sQuery(id+"F0.wireOp",EDGE,"E65");Q48=makeQuery(id+"F0.imprint","IMPRINT",FACE,{"disambiguationData":[TD([[makeQuery(id+"F0.imprint","IMPRINT",EDGE,{"derivedFrom":subQ0}),-1.0]])]});}
            var Q49;
            {var subQ0=sQuery(id+"F0.wireOp",EDGE,"E67");Q49=makeQuery(id+"F0.imprint","IMPRINT",FACE,{"disambiguationData":[TD([[makeQuery(id+"F0.imprint","IMPRINT",EDGE,{"derivedFrom":subQ0}),-1.0]])]});}
            var Q50;
            {var subQ0=sQuery(id+"F0.wireOp",EDGE,"E62");Q50=makeQuery(id+"F0.imprint","IMPRINT",FACE,{"disambiguationData":[TD([[makeQuery(id+"F0.imprint","IMPRINT",EDGE,{"derivedFrom":subQ0}),-1.0]])]});}
            var Q51;
            {var subQ0=sQuery(id+"F0.wireOp",EDGE,"E22");Q51=makeQuery(id+"F0.imprint","IMPRINT",FACE,{"disambiguationData":[TD([[makeQuery(id+"F0.imprint","IMPRINT",EDGE,{"derivedFrom":subQ0}),1.0]])]});}
            var Q52;
            {var subQ0=sQuery(id+"F0.wireOp",EDGE,"E69");Q52=makeQuery(id+"F0.imprint","IMPRINT",FACE,{"disambiguationData":[TD([[makeQuery(id+"F0.imprint","IMPRINT",EDGE,{"derivedFrom":subQ0}),-1.0]])]});}
            var Q53;
            {var subQ0=sQuery(id+"F0.wireOp",EDGE,"E64");Q53=makeQuery(id+"F0.imprint","IMPRINT",FACE,{"disambiguationData":[TD([[makeQuery(id+"F0.imprint","IMPRINT",EDGE,{"derivedFrom":subQ0}),-1.0]])]});}
            var Q54;
            {var subQ0=sQuery(id+"F0.wireOp",EDGE,"E22");Q54=makeQuery(id+"F0.imprint","IMPRINT",FACE,{"disambiguationData":[TD([[makeQuery(id+"F0.imprint","IMPRINT",EDGE,{"derivedFrom":subQ0}),-1.0]])]});}
            var Q55;
            {var subQ0=sQuery(id+"F0.wireOp",EDGE,"E63");Q55=makeQuery(id+"F0.imprint","IMPRINT",FACE,{"disambiguationData":[TD([[makeQuery(id+"F0.imprint","IMPRINT",EDGE,{"derivedFrom":subQ0}),-1.0]])]});}
            var Q56;
            {var subQ7=sQuery(id+"F0.wireOp",EDGE,"E72");Q56=makeQuery(id+"F0.imprint","IMPRINT",FACE,{"disambiguationData":[TD([[makeQuery(id+"F0.imprint","IMPRINT",EDGE,{"derivedFrom":subQ7}),-1.0]])]});}
            var Q57;
            {var subQ3=sQuery(id+"F0.wireOp",EDGE,"E42");Q57=makeQuery(id+"F0.imprint","IMPRINT",FACE,{"disambiguationData":[TD([[makeQuery(id+"F0.imprint","IMPRINT",EDGE,{"derivedFrom":subQ3}),-1.0]])]});}
            var Q58;
            {var subQ3=sQuery(id+"F0.wireOp",EDGE,"E61");Q58=makeQuery(id+"F0.imprint","IMPRINT",FACE,{"disambiguationData":[TD([[makeQuery(id+"F0.imprint","IMPRINT",EDGE,{"derivedFrom":subQ3}),-1.0]])]});}
            var Q59;
            {var subQ0=sQuery(id+"F0.wireOp",EDGE,"E70");Q59=makeQuery(id+"F0.imprint","IMPRINT",FACE,{"disambiguationData":[TD([[makeQuery(id+"F0.imprint","IMPRINT",EDGE,{"derivedFrom":subQ0}),-1.0]])]});}
            var Q60;
            {var subQ0=sQuery(id+"F0.wireOp",EDGE,"E68");Q60=makeQuery(id+"F0.imprint","IMPRINT",FACE,{"disambiguationData":[TD([[makeQuery(id+"F0.imprint","IMPRINT",EDGE,{"derivedFrom":subQ0}),-1.0]])]});}
            var Q61;
            {var subQ0=sQuery(id+"F0.wireOp",EDGE,"E170");Q61=makeQuery(id+"F0.imprint","IMPRINT",FACE,{"disambiguationData":[TD([[makeQuery(id+"F0.imprint","IMPRINT",EDGE,{"derivedFrom":subQ0}),-1.0]])]});}
            var Q62;
            {var subQ0=sQuery(id+"F0.wireOp",EDGE,"E66");Q62=makeQuery(id+"F0.imprint","IMPRINT",FACE,{"disambiguationData":[TD([[makeQuery(id+"F0.imprint","IMPRINT",EDGE,{"derivedFrom":subQ0}),-1.0]])]});}
            var Q63;
            {var subQ0=sQuery(id+"F0.wireOp",EDGE,"E71");Q63=makeQuery(id+"F0.imprint","IMPRINT",FACE,{"disambiguationData":[TD([[makeQuery(id+"F0.imprint","IMPRINT",EDGE,{"derivedFrom":subQ0}),-1.0]])]});}
            var Q64;
            {var subQ7=sQuery(id+"F0.wireOp",EDGE,"E177");Q64=makeQuery(id+"F0.imprint","IMPRINT",FACE,{"disambiguationData":[TD([[makeQuery(id+"F0.imprint","IMPRINT",EDGE,{"derivedFrom":subQ7}),-1.0]])]});}
            var Q65;
            {var subQ5=sQuery(id+"F0.wireOp",EDGE,"E285");Q65=makeQuery(id+"F0.imprint","IMPRINT",FACE,{"disambiguationData":[TD([[makeQuery(id+"F0.imprint","IMPRINT",EDGE,{"derivedFrom":subQ5}),1.0]])]});}
            var Q66;
            {var subQ5=sQuery(id+"F0.wireOp",EDGE,"E288");Q66=makeQuery(id+"F0.imprint","IMPRINT",FACE,{"disambiguationData":[TD([[makeQuery(id+"F0.imprint","IMPRINT",EDGE,{"derivedFrom":subQ5}),1.0]])]});}
            var Q67;
            {var subQ1=sQuery(id+"F0.wireOp",EDGE,"E170");Q67=makeQuery(id+"F0.imprint","IMPRINT",FACE,{"disambiguationData":[TD([[makeQuery(id+"F0.imprint","IMPRINT",EDGE,{"derivedFrom":subQ1}),1.0]])]});}
            var Q68;
            Q68=makeQuery(id+"F0.imprint","IMPRINT",FACE,{"disambiguationData":[TD([[makeQuery(id+"F0.imprint","IMPRINT",EDGE,{"derivedFrom":sQuery(id+"F0.wireOp",EDGE,"E40")}),-1.0]])]});
            var Q69;
            Q69=makeQuery(id+"F0.imprint","IMPRINT",FACE,{"disambiguationData":[TD([[makeQuery(id+"F0.imprint","IMPRINT",EDGE,{"derivedFrom":sQuery(id+"F0.wireOp",EDGE,"E59")}),1.0]])]});
            var Q70;
            {var subQ5=sQuery(id+"F0.wireOp",EDGE,"E286");Q70=makeQuery(id+"F0.imprint","IMPRINT",FACE,{"disambiguationData":[TD([[makeQuery(id+"F0.imprint","IMPRINT",EDGE,{"derivedFrom":subQ5}),-1.0]])]});}
            var Q71;
            {var subQ1=sQuery(id+"F0.wireOp",EDGE,"E177");Q71=makeQuery(id+"F0.imprint","IMPRINT",FACE,{"disambiguationData":[TD([[makeQuery(id+"F0.imprint","IMPRINT",EDGE,{"derivedFrom":subQ1}),1.0]])]});}
            var Q72;
            {var subQ5=sQuery(id+"F0.wireOp",EDGE,"E287");Q72=makeQuery(id+"F0.imprint","IMPRINT",FACE,{"disambiguationData":[TD([[makeQuery(id+"F0.imprint","IMPRINT",EDGE,{"derivedFrom":subQ5}),-1.0]])]});}
            var Q73;
            {var subQ3=sQuery(id+"F0.wireOp",EDGE,"E214");Q73=makeQuery(id+"F0.imprint","IMPRINT",FACE,{"disambiguationData":[TD([[makeQuery(id+"F0.imprint","IMPRINT",EDGE,{"derivedFrom":subQ3}),1.0]])]});}
            var Q74;
            Q74=makeQuery(id+"F0.imprint","IMPRINT",FACE,{"disambiguationData":[TD([[makeQuery(id+"F0.imprint","IMPRINT",EDGE,{"derivedFrom":sQuery(id+"F0.wireOp",EDGE,"E178")}),1.0]])]});
            var Q75;
            {var subQ2=sQuery(id+"F0.wireOp",EDGE,"E210");Q75=makeQuery(id+"F0.imprint","IMPRINT",FACE,{"disambiguationData":[TD([[makeQuery(id+"F0.imprint","IMPRINT",EDGE,{"derivedFrom":subQ2}),1.0]])]});}
            var Q76;
            Q76=makeQuery(id+"F0.imprint","IMPRINT",FACE,{"disambiguationData":[TD([[makeQuery(id+"F0.imprint","IMPRINT",EDGE,{"derivedFrom":sQuery(id+"F0.wireOp",EDGE,"E213")}),1.0]])]});
            var Q77;
            {var subQ1=sQuery(id+"F0.wireOp",EDGE,"E215");Q77=makeQuery(id+"F0.imprint","IMPRINT",FACE,{"disambiguationData":[TD([[makeQuery(id+"F0.imprint","IMPRINT",EDGE,{"derivedFrom":subQ1}),1.0]])]});}
            var Q78;
            Q78=makeQuery(id+"F0.imprint","IMPRINT",FACE,{"disambiguationData":[TD([[makeQuery(id+"F0.imprint","IMPRINT",EDGE,{"derivedFrom":sQuery(id+"F0.wireOp",EDGE,"E223")}),-1.0]])]});
            var Q79;
            {var subQ4=sQuery(id+"F0.wireOp",EDGE,"E208");Q79=makeQuery(id+"F0.imprint","IMPRINT",FACE,{"disambiguationData":[TD([[makeQuery(id+"F0.imprint","IMPRINT",EDGE,{"derivedFrom":subQ4}),1.0]])]});}
            var Q80;
            Q80=makeQuery(id+"F0.imprint","IMPRINT",FACE,{"disambiguationData":[TD([[makeQuery(id+"F0.imprint","IMPRINT",EDGE,{"derivedFrom":sQuery(id+"F0.wireOp",EDGE,"E171")}),1.0]])]});
            var Q81;
            {var subQ0=sQuery(id+"F0.wireOp",EDGE,"E29");Q81=makeQuery(id+"F0.imprint","IMPRINT",FACE,{"disambiguationData":[TD([[makeQuery(id+"F0.imprint","IMPRINT",EDGE,{"derivedFrom":subQ0}),1.0]])]});}
            var Q82;
            {var subQ0=sQuery(id+"F0.wireOp",EDGE,"E26");Q82=makeQuery(id+"F0.imprint","IMPRINT",FACE,{"disambiguationData":[TD([[makeQuery(id+"F0.imprint","IMPRINT",EDGE,{"derivedFrom":subQ0}),-1.0]])]});}
            var Q83;
            {var subQ0=sQuery(id+"F0.wireOp",EDGE,"E35");Q83=makeQuery(id+"F0.imprint","IMPRINT",FACE,{"disambiguationData":[TD([[makeQuery(id+"F0.imprint","IMPRINT",EDGE,{"derivedFrom":subQ0}),-1.0]])]});}
            var Q84;
            {var subQ0=sQuery(id+"F0.wireOp",EDGE,"E29");Q84=makeQuery(id+"F0.imprint","IMPRINT",FACE,{"disambiguationData":[TD([[makeQuery(id+"F0.imprint","IMPRINT",EDGE,{"derivedFrom":subQ0}),-1.0]])]});}
            var Q85;
            {var subQ0=sQuery(id+"F0.wireOp",EDGE,"E32");Q85=makeQuery(id+"F0.imprint","IMPRINT",FACE,{"disambiguationData":[TD([[makeQuery(id+"F0.imprint","IMPRINT",EDGE,{"derivedFrom":subQ0}),1.0]])]});}
            var Q86;
            {var subQ0=sQuery(id+"F0.wireOp",EDGE,"E35");Q86=makeQuery(id+"F0.imprint","IMPRINT",FACE,{"disambiguationData":[TD([[makeQuery(id+"F0.imprint","IMPRINT",EDGE,{"derivedFrom":subQ0}),1.0]])]});}
            var Q87;
            {var subQ0=sQuery(id+"F0.wireOp",EDGE,"E38");Q87=makeQuery(id+"F0.imprint","IMPRINT",FACE,{"disambiguationData":[TD([[makeQuery(id+"F0.imprint","IMPRINT",EDGE,{"derivedFrom":subQ0}),1.0]])]});}
            var Q88;
            {var subQ0=sQuery(id+"F0.wireOp",EDGE,"E23");Q88=makeQuery(id+"F0.imprint","IMPRINT",FACE,{"disambiguationData":[TD([[makeQuery(id+"F0.imprint","IMPRINT",EDGE,{"derivedFrom":subQ0}),-1.0]])]});}
            var Q89;
            {var subQ0=sQuery(id+"F0.wireOp",EDGE,"E26");Q89=makeQuery(id+"F0.imprint","IMPRINT",FACE,{"disambiguationData":[TD([[makeQuery(id+"F0.imprint","IMPRINT",EDGE,{"derivedFrom":subQ0}),1.0]])]});}
            var Q90;
            {var subQ0=sQuery(id+"F0.wireOp",EDGE,"E32");Q90=makeQuery(id+"F0.imprint","IMPRINT",FACE,{"disambiguationData":[TD([[makeQuery(id+"F0.imprint","IMPRINT",EDGE,{"derivedFrom":subQ0}),-1.0]])]});}
            var Q91;
            {var subQ0=sQuery(id+"F0.wireOp",EDGE,"E38");Q91=makeQuery(id+"F0.imprint","IMPRINT",FACE,{"disambiguationData":[TD([[makeQuery(id+"F0.imprint","IMPRINT",EDGE,{"derivedFrom":subQ0}),-1.0]])]});}
            var Q92;
            Q92=makeQuery(id+"F0.imprint","IMPRINT",FACE,{"disambiguationData":[TD([[makeQuery(id+"F0.imprint","IMPRINT",EDGE,{"derivedFrom":sQuery(id+"F0.wireOp",EDGE,"E4")}),-1.0]])]});
            extrude(context, id + "F2", {"entities" : qUnion([Q0, Q1, Q2, Q3, Q4, Q5, Q6, Q7, Q8, Q9, Q10, Q11, Q12, Q13, Q14, Q15, Q16, Q17, Q18, Q19, Q20, Q21, Q22, Q23, Q24, Q25, Q26, Q27, Q28, Q29, Q30, Q31, Q32, Q33, Q34, Q35, Q36, Q37, Q38, Q39, Q40, Q41, Q42, Q43, Q44, Q45, Q46, Q47, Q48, Q49, Q50, Q51, Q52, Q53, Q54, Q55, Q56, Q57, Q58, Q59, Q60, Q61, Q62, Q63, Q64, Q65, Q66, Q67, Q68, Q69, Q70, Q71, Q72, Q73, Q74, Q75, Q76, Q77, Q78, Q79, Q80, Q81, Q82, Q83, Q84, Q85, Q86, Q87, Q88, Q89, Q90, Q91, Q92]), "depth" : 77 * mm + 1.6 * mm});
        }
        {
            var Q0;
            {var subQ1=sQuery(id+"F0.wireOp",EDGE,"E170");Q0=makeQuery(id+"F0.imprint","IMPRINT",FACE,{"disambiguationData":[TD([[makeQuery(id+"F0.imprint","IMPRINT",EDGE,{"derivedFrom":subQ1}),-1.0]])]});}
            var Q1;
            {var subQ0=sQuery(id+"F0.wireOp",EDGE,"E72");Q1=makeQuery(id+"F0.imprint","IMPRINT",FACE,{"disambiguationData":[TD([[makeQuery(id+"F0.imprint","IMPRINT",EDGE,{"derivedFrom":subQ0}),-1.0]])]});}
            var Q2;
            {var subQ3=sQuery(id+"F0.wireOp",EDGE,"E42");Q2=makeQuery(id+"F0.imprint","IMPRINT",FACE,{"disambiguationData":[TD([[makeQuery(id+"F0.imprint","IMPRINT",EDGE,{"derivedFrom":subQ3}),-1.0]])]});}
            var Q3;
            {var subQ0=sQuery(id+"F0.wireOp",EDGE,"E71");Q3=makeQuery(id+"F0.imprint","IMPRINT",FACE,{"disambiguationData":[TD([[makeQuery(id+"F0.imprint","IMPRINT",EDGE,{"derivedFrom":subQ0}),-1.0]])]});}
            var Q4;
            {var subQ5=sQuery(id+"F0.wireOp",EDGE,"E70");Q4=makeQuery(id+"F0.imprint","IMPRINT",FACE,{"disambiguationData":[TD([[makeQuery(id+"F0.imprint","IMPRINT",EDGE,{"derivedFrom":subQ5}),-1.0]])]});}
            var Q5;
            {var subQ0=sQuery(id+"F0.wireOp",EDGE,"E69");Q5=makeQuery(id+"F0.imprint","IMPRINT",FACE,{"disambiguationData":[TD([[makeQuery(id+"F0.imprint","IMPRINT",EDGE,{"derivedFrom":subQ0}),-1.0]])]});}
            var Q6;
            {var subQ0=sQuery(id+"F0.wireOp",EDGE,"E68");Q6=makeQuery(id+"F0.imprint","IMPRINT",FACE,{"disambiguationData":[TD([[makeQuery(id+"F0.imprint","IMPRINT",EDGE,{"derivedFrom":subQ0}),-1.0]])]});}
            var Q7;
            {var subQ4=sQuery(id+"F0.wireOp",EDGE,"E66");Q7=makeQuery(id+"F0.imprint","IMPRINT",FACE,{"disambiguationData":[TD([[makeQuery(id+"F0.imprint","IMPRINT",EDGE,{"derivedFrom":subQ4}),-1.0]])]});}
            var Q8;
            {var subQ0=sQuery(id+"F0.wireOp",EDGE,"E67");Q8=makeQuery(id+"F0.imprint","IMPRINT",FACE,{"disambiguationData":[TD([[makeQuery(id+"F0.imprint","IMPRINT",EDGE,{"derivedFrom":subQ0}),-1.0]])]});}
            var Q9;
            {var subQ0=sQuery(id+"F0.wireOp",EDGE,"E65");Q9=makeQuery(id+"F0.imprint","IMPRINT",FACE,{"disambiguationData":[TD([[makeQuery(id+"F0.imprint","IMPRINT",EDGE,{"derivedFrom":subQ0}),-1.0]])]});}
            var Q10;
            {var subQ5=sQuery(id+"F0.wireOp",EDGE,"E285");Q10=makeQuery(id+"F0.imprint","IMPRINT",FACE,{"disambiguationData":[TD([[makeQuery(id+"F0.imprint","IMPRINT",EDGE,{"derivedFrom":subQ5}),1.0]])]});}
            var Q11;
            {var subQ5=sQuery(id+"F0.wireOp",EDGE,"E288");Q11=makeQuery(id+"F0.imprint","IMPRINT",FACE,{"disambiguationData":[TD([[makeQuery(id+"F0.imprint","IMPRINT",EDGE,{"derivedFrom":subQ5}),1.0]])]});}
            var Q12;
            {var subQ3=sQuery(id+"F0.wireOp",EDGE,"E214");Q12=makeQuery(id+"F0.imprint","IMPRINT",FACE,{"disambiguationData":[TD([[makeQuery(id+"F0.imprint","IMPRINT",EDGE,{"derivedFrom":subQ3}),1.0]])]});}
            var Q13;
            {var subQ0=sQuery(id+"F0.wireOp",EDGE,"E64");Q13=makeQuery(id+"F0.imprint","IMPRINT",FACE,{"disambiguationData":[TD([[makeQuery(id+"F0.imprint","IMPRINT",EDGE,{"derivedFrom":subQ0}),-1.0]])]});}
            var Q14;
            {var subQ0=sQuery(id+"F0.wireOp",EDGE,"E63");Q14=makeQuery(id+"F0.imprint","IMPRINT",FACE,{"disambiguationData":[TD([[makeQuery(id+"F0.imprint","IMPRINT",EDGE,{"derivedFrom":subQ0}),-1.0]])]});}
            var Q15;
            {var subQ4=sQuery(id+"F0.wireOp",EDGE,"E62");Q15=makeQuery(id+"F0.imprint","IMPRINT",FACE,{"disambiguationData":[TD([[makeQuery(id+"F0.imprint","IMPRINT",EDGE,{"derivedFrom":subQ4}),-1.0]])]});}
            var Q16;
            {var subQ8=sQuery(id+"F0.wireOp",EDGE,"E61");Q16=makeQuery(id+"F0.imprint","IMPRINT",FACE,{"disambiguationData":[TD([[makeQuery(id+"F0.imprint","IMPRINT",EDGE,{"derivedFrom":subQ8}),-1.0]])]});}
            var Q17;
            {var subQ6=sQuery(id+"F0.wireOp",EDGE,"E177");Q17=makeQuery(id+"F0.imprint","IMPRINT",FACE,{"disambiguationData":[TD([[makeQuery(id+"F0.imprint","IMPRINT",EDGE,{"derivedFrom":subQ6}),-1.0]])]});}
            var Q18;
            {var subQ5=sQuery(id+"F0.wireOp",EDGE,"E287");Q18=makeQuery(id+"F0.imprint","IMPRINT",FACE,{"disambiguationData":[TD([[makeQuery(id+"F0.imprint","IMPRINT",EDGE,{"derivedFrom":subQ5}),-1.0]])]});}
            var Q19;
            {var subQ5=sQuery(id+"F0.wireOp",EDGE,"E286");Q19=makeQuery(id+"F0.imprint","IMPRINT",FACE,{"disambiguationData":[TD([[makeQuery(id+"F0.imprint","IMPRINT",EDGE,{"derivedFrom":subQ5}),-1.0]])]});}
            var Q20;
            Q20=makeQuery(id+"F0.imprint","IMPRINT",FACE,{"disambiguationData":[TD([[makeQuery(id+"F0.imprint","IMPRINT",EDGE,{"derivedFrom":sQuery(id+"F0.wireOp",EDGE,"E59")}),1.0]])]});
            var Q21;
            Q21=makeQuery(id+"F0.imprint","IMPRINT",FACE,{"disambiguationData":[TD([[makeQuery(id+"F0.imprint","IMPRINT",EDGE,{"derivedFrom":sQuery(id+"F0.wireOp",EDGE,"E40")}),-1.0]])]});
            var Q22;
            Q22=makeQuery(id+"F0.imprint","IMPRINT",FACE,{"disambiguationData":[TD([[makeQuery(id+"F0.imprint","IMPRINT",EDGE,{"derivedFrom":sQuery(id+"F0.wireOp",EDGE,"E113")}),-1.0]])]});
            var Q23;
            {var subQ3=sQuery(id+"F0.wireOp",EDGE,"E128");Q23=makeQuery(id+"F0.imprint","IMPRINT",FACE,{"disambiguationData":[TD([[makeQuery(id+"F0.imprint","IMPRINT",EDGE,{"derivedFrom":subQ3}),1.0]])]});}
            var Q24;
            {var subQ1=sQuery(id+"F0.wireOp",EDGE,"E86");Q24=makeQuery(id+"F0.imprint","IMPRINT",FACE,{"disambiguationData":[TD([[makeQuery(id+"F0.imprint","IMPRINT",EDGE,{"derivedFrom":subQ1}),1.0]])]});}
            var Q25;
            {var subQ4=sQuery(id+"F0.wireOp",EDGE,"E98");Q25=makeQuery(id+"F0.imprint","IMPRINT",FACE,{"disambiguationData":[TD([[makeQuery(id+"F0.imprint","IMPRINT",EDGE,{"derivedFrom":subQ4}),1.0]])]});}
            var Q26;
            {var subQ2=sQuery(id+"F0.wireOp",EDGE,"E97");Q26=makeQuery(id+"F0.imprint","IMPRINT",FACE,{"disambiguationData":[TD([[makeQuery(id+"F0.imprint","IMPRINT",EDGE,{"derivedFrom":subQ2}),1.0]])]});}
            var Q27;
            {var subQ7=sQuery(id+"F0.wireOp",EDGE,"E96");Q27=makeQuery(id+"F0.imprint","IMPRINT",FACE,{"disambiguationData":[TD([[makeQuery(id+"F0.imprint","IMPRINT",EDGE,{"derivedFrom":subQ7}),1.0]])]});}
            var Q28;
            {var subQ1=sQuery(id+"F0.wireOp",EDGE,"E95");Q28=makeQuery(id+"F0.imprint","IMPRINT",FACE,{"disambiguationData":[TD([[makeQuery(id+"F0.imprint","IMPRINT",EDGE,{"derivedFrom":subQ1}),1.0]])]});}
            var Q29;
            {var subQ4=sQuery(id+"F0.wireOp",EDGE,"E94");Q29=makeQuery(id+"F0.imprint","IMPRINT",FACE,{"disambiguationData":[TD([[makeQuery(id+"F0.imprint","IMPRINT",EDGE,{"derivedFrom":subQ4}),1.0]])]});}
            var Q30;
            {var subQ1=sQuery(id+"F0.wireOp",EDGE,"E93");Q30=makeQuery(id+"F0.imprint","IMPRINT",FACE,{"disambiguationData":[TD([[makeQuery(id+"F0.imprint","IMPRINT",EDGE,{"derivedFrom":subQ1}),1.0]])]});}
            var Q31;
            {var subQ3=sQuery(id+"F0.wireOp",EDGE,"E92");Q31=makeQuery(id+"F0.imprint","IMPRINT",FACE,{"disambiguationData":[TD([[makeQuery(id+"F0.imprint","IMPRINT",EDGE,{"derivedFrom":subQ3}),1.0]])]});}
            var Q32;
            {var subQ1=sQuery(id+"F0.wireOp",EDGE,"E91");Q32=makeQuery(id+"F0.imprint","IMPRINT",FACE,{"disambiguationData":[TD([[makeQuery(id+"F0.imprint","IMPRINT",EDGE,{"derivedFrom":subQ1}),1.0]])]});}
            var Q33;
            {var subQ3=sQuery(id+"F0.wireOp",EDGE,"E90");Q33=makeQuery(id+"F0.imprint","IMPRINT",FACE,{"disambiguationData":[TD([[makeQuery(id+"F0.imprint","IMPRINT",EDGE,{"derivedFrom":subQ3}),1.0]])]});}
            var Q34;
            {var subQ1=sQuery(id+"F0.wireOp",EDGE,"E89");Q34=makeQuery(id+"F0.imprint","IMPRINT",FACE,{"disambiguationData":[TD([[makeQuery(id+"F0.imprint","IMPRINT",EDGE,{"derivedFrom":subQ1}),1.0]])]});}
            var Q35;
            {var subQ4=sQuery(id+"F0.wireOp",EDGE,"E88");Q35=makeQuery(id+"F0.imprint","IMPRINT",FACE,{"disambiguationData":[TD([[makeQuery(id+"F0.imprint","IMPRINT",EDGE,{"derivedFrom":subQ4}),1.0]])]});}
            var Q36;
            {var subQ1=sQuery(id+"F0.wireOp",EDGE,"E87");Q36=makeQuery(id+"F0.imprint","IMPRINT",FACE,{"disambiguationData":[TD([[makeQuery(id+"F0.imprint","IMPRINT",EDGE,{"derivedFrom":subQ1}),1.0]])]});}
            extrude(context, id + "F3", {"entities" : qUnion([Q0, Q1, Q2, Q3, Q4, Q5, Q6, Q7, Q8, Q9, Q10, Q11, Q12, Q13, Q14, Q15, Q16, Q17, Q18, Q19, Q20, Q21, Q22, Q23, Q24, Q25, Q26, Q27, Q28, Q29, Q30, Q31, Q32, Q33, Q34, Q35, Q36]), "depth" : (1.6 + 77 + 8) * mm});
        }
        {
            var Q0;
            Q0=makeQuery(id+"F2.opExtrude","SWEPT_EDGE",EDGE,{"disambiguationData":[OSD([sQuery(id+"F0.wireOp",EDGE,"E4"),sQuery(id+"F0.wireOp",EDGE,"E13")])]});
            var Q1;
            Q1=makeQuery(id+"F2.opExtrude","SWEPT_EDGE",EDGE,{"disambiguationData":[OSD([sQuery(id+"F0.wireOp",EDGE,"E4"),sQuery(id+"F0.wireOp",EDGE,"E10")])]});
            var Q2;
            Q2=makeQuery(id+"F2.opExtrude","SWEPT_EDGE",EDGE,{"disambiguationData":[OSD([sQuery(id+"F0.wireOp",EDGE,"E1"),sQuery(id+"F0.wireOp",EDGE,"E2")])]});
            var Q3;
            Q3=makeQuery(id+"F2.opExtrude","SWEPT_EDGE",EDGE,{"disambiguationData":[OSD([sQuery(id+"F0.wireOp",EDGE,"E2"),sQuery(id+"F0.wireOp",EDGE,"E3")])]});
            var Q4;
            Q4=makeQuery(id+"F2.opExtrude","CAP_EDGE",EDGE,{"disambiguationData":[OSD([sQuery(id+"F0.wireOp",EDGE,"E3")])],"isStart":false});
            var Q5;
            Q5=makeQuery(id+"F2.opExtrude","CAP_EDGE",EDGE,{"disambiguationData":[OSD([sQuery(id+"F0.wireOp",EDGE,"E4")])],"isStart":false});
            var Q6;
            Q6=makeQuery(id+"F2.opExtrude","CAP_EDGE",EDGE,{"disambiguationData":[OSD([sQuery(id+"F0.wireOp",EDGE,"E1")])],"isStart":false});
            var Q7;
            Q7=makeQuery(id+"F2.opExtrude","CAP_EDGE",EDGE,{"disambiguationData":[OSD([sQuery(id+"F0.wireOp",EDGE,"E2")])],"isStart":false});
            chamfer(context, id + "F4", {"entities" : qUnion([Q0, Q1, Q2, Q3, Q4, Q5, Q6, Q7]), "width" : 5 * mm});
        }
    });
